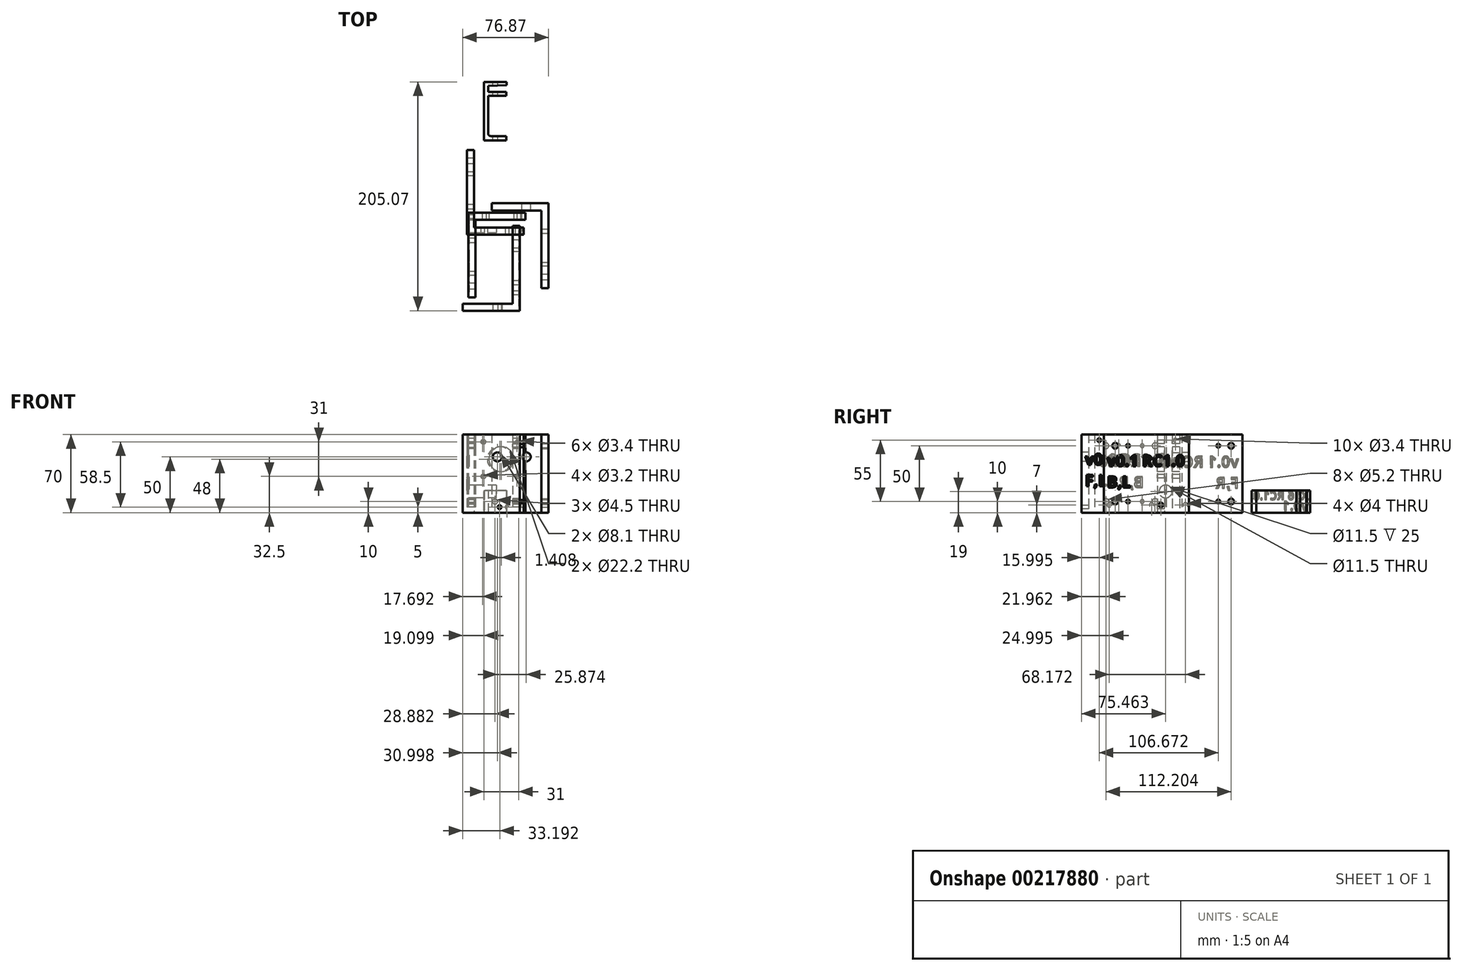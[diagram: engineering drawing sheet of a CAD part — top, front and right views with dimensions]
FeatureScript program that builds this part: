
annotation { "Feature Type Name" : "Feature", "Feature Type Description" : "" }
export const myFeature = defineFeature(function(context is Context, id is Id, definition is map)
    precondition{}
    {
        {
            var Q0;
            Q0=qCreatedBy(makeId("Top.planeOp"),FACE);
            var sketch = newSketch(context, id + "F0", { "sketchPlane" : qUnion([Q0])});
            skLineSegment(sketch, "E0.bottom", {"start": v(-23.8, 33.14) * mm, "end": v(-43.8, 33.14) * mm});
            skLineSegment(sketch, "E0.top", {"start": v(-23.8, 37.14) * mm, "end": v(-43.8, 37.14) * mm});
            skLineSegment(sketch, "E0.left", {"start": v(-23.8, 33.14) * mm, "end": v(-23.8, 37.14) * mm});
            skLineSegment(sketch, "E0.right", {"start": v(-43.8, 33.14) * mm, "end": v(-43.8, 37.14) * mm});
            skLineSegment(sketch, "E1.bottom", {"start": v(-43.8, 37.14) * mm, "end": v(-39.8, 37.14) * mm});
            skLineSegment(sketch, "E1.top", {"start": v(-43.8, 73.14) * mm, "end": v(-39.8, 73.14) * mm});
            skLineSegment(sketch, "E1.left", {"start": v(-43.8, 37.14) * mm, "end": v(-43.8, 73.14) * mm});
            skLineSegment(sketch, "E1.right", {"start": v(-39.8, 37.14) * mm, "end": v(-39.8, 73.14) * mm});
            skLineSegment(sketch, "E2.bottom", {"start": v(-43.8, 73.14) * mm, "end": v(-23.8, 73.14) * mm});
            skLineSegment(sketch, "E2.top", {"start": v(-43.8, 77.14) * mm, "end": v(-39.8, 77.14) * mm});
            skLineSegment(sketch, "E2.left", {"start": v(-43.8, 73.14) * mm, "end": v(-43.8, 77.14) * mm});
            skLineSegment(sketch, "E2.right", {"start": v(-23.8, 73.14) * mm, "end": v(-23.8, 77.14) * mm});
            skLineSegment(sketch, "E3.top", {"start": v(-43.8, 82.64) * mm, "end": v(-39.8, 82.64) * mm});
            skLineSegment(sketch, "E3.left", {"start": v(-43.8, 77.14) * mm, "end": v(-43.8, 82.64) * mm});
            skLineSegment(sketch, "E3.right", {"start": v(-39.8, 77.14) * mm, "end": v(-39.8, 82.64) * mm});
            skLineSegment(sketch, "E4.top", {"start": v(-43.8, 85.63) * mm, "end": v(-39.8, 85.63) * mm});
            skLineSegment(sketch, "E4.left", {"start": v(-43.8, 82.64) * mm, "end": v(-43.8, 85.63) * mm});
            skLineSegment(sketch, "E4.right", {"start": v(-39.8, 82.64) * mm, "end": v(-39.8, 85.63) * mm});
            skLineSegment(sketch, "E5", {"start": v(-39.8, 77.14) * mm, "end": v(-39.8, 81.94) * mm});
            skLineSegment(sketch, "E6", {"start": v(-39.8, 81.94) * mm, "end": v(-23.3, 82.64) * mm});
            skLineSegment(sketch, "E7", {"start": v(-23.3, 82.64) * mm, "end": v(-23.42, 85.63) * mm});
            skLineSegment(sketch, "E8", {"start": v(-23.42, 85.63) * mm, "end": v(-39.8, 85.63) * mm});
            skLineSegment(sketch, "E9.top", {"start": v(-23.8, 76.74) * mm, "end": v(-39.8, 76.74) * mm});
            skLineSegment(sketch, "E9.left", {"start": v(-23.8, 77.14) * mm, "end": v(-23.8, 76.74) * mm});
            skLineSegment(sketch, "E9.right", {"start": v(-39.8, 77.14) * mm, "end": v(-39.8, 76.74) * mm});
            skSolve(sketch);
        }
        {
            var Q0;
            Q0 = qSketchRegion(id + "F0", true);
            extrude(context, id + "F1", {"entities" : qUnion([Q0]), "depth" : 20 * mm});
        }
        {
            var Q0;
            Q0=makeQuery(id+"F1.opExtrude","SWEPT_FACE",FACE,{"disambiguationData":[OSD([sQuery(id+"F0.wireOp",EDGE,"E0.bottom")])]});
            var sketch = newSketch(context, id + "F2", { "sketchPlane" : qUnion([Q0])});
            skLineSegment(sketch, "E10", {"start": v(-33.8, 20) * mm, "end": v(-33.8, 10) * mm, "construction": true});
            skPoint(sketch, "E10.endSnap0", {"position": v(-23.8, 10) * mm});
            skCircle(sketch, "E11", {"center": v(-33.8, 10) * mm, "radius": 2.25 * mm});
            skSolve(sketch);
        }
        {
            var Q0;
            Q0 = qSketchRegion(id + "F2", true);
            extrude(context, id + "F3", {"entities" : qUnion([Q0]), "operationType" : NewBodyOperationType.REMOVE, "oppositeDirection" : true, "depth" : 200 * mm});
        }
        {
            var Q0;
            Q0=makeQuery(id+"F1.opExtrude","SWEPT_FACE",FACE,{"disambiguationData":[OSD([sQuery(id+"F0.wireOp",EDGE,"E0.right"),sQuery(id+"F0.wireOp",EDGE,"E1.left"),sQuery(id+"F0.wireOp",EDGE,"E2.left"),sQuery(id+"F0.wireOp",EDGE,"E3.left"),sQuery(id+"F0.wireOp",EDGE,"E4.left")])]});
            var sketch = newSketch(context, id + "F4", { "sketchPlane" : qUnion([Q0])});
            skText(sketch, "E12", { "text": "X16 RC1.0\n", "fontName": "OpenSans-Bold.ttf"});
            const initialGuessF4  = {"E12": [-0.08421, 0.01155, 1, 0, 0.00747]};
            skSetInitialGuess(sketch, initialGuessF4);
            skSolve(sketch);
        }
        {
            var Q0;
            Q0 = qSketchRegion(id + "F4", true);
            extrude(context, id + "F5", {"entities" : qUnion([Q0]), "operationType" : NewBodyOperationType.REMOVE, "oppositeDirection" : true, "depth" : .5 * mm});
        }
        {
            var Q0;
            {var subQ6=sQuery(id+"F0.wireOp",EDGE,"E4.left");var subQ8=sQuery(id+"F0.wireOp",EDGE,"E3.left");var subQ10=sQuery(id+"F0.wireOp",EDGE,"E2.left");var subQ13=sQuery(id+"F0.wireOp",EDGE,"E1.left");var subQ14=sQuery(id+"F0.wireOp",EDGE,"E0.right");var subQ17=sQuery(id+"F0.wireOp",EDGE,"E0.bottom");Q0=makeQuery(id+"F5.boolean.opBoolean","SPLIT",FACE,{"disambiguationData":[TD([makeQuery(id+"F1.opExtrude","SWEPT_FACE",FACE,{"disambiguationData":[OSD([subQ17])]})])],"derivedFrom":makeQuery(id+"F1.opExtrude","SWEPT_FACE",FACE,{"disambiguationData":[OSD([subQ14,subQ13,subQ10,subQ8,subQ6])]})});}
            var sketch = newSketch(context, id + "F6", { "sketchPlane" : qUnion([Q0])});
            skText(sketch, "E13", { "text": "v0.1", "fontName": "OpenSans-Bold.ttf"});
            const initialGuessF6  = {"E13": [-0.0841, 0.0019, 1, 0, 0.00852]};
            skSetInitialGuess(sketch, initialGuessF6);
            skSolve(sketch);
        }
        {
            var Q0;
            Q0 = qSketchRegion(id + "F6", true);
            extrude(context, id + "F7", {"entities" : qUnion([Q0]), "operationType" : NewBodyOperationType.REMOVE, "oppositeDirection" : true, "depth" : .5 * mm});
        }
        {
            var Q0;
            Q0=makeQuery(id+"F5.boolean.opBoolean","COPY",FACE,{"derivedFrom":makeQuery(id+"F5.opExtrude","CAP_FACE",FACE,{"disambiguationData":[OSD([sQuery(id+"F4.wireOp",EDGE,"E12.sketch_text.stroke-0"),sQuery(id+"F4.wireOp",EDGE,"E12.sketch_text.stroke-1"),sQuery(id+"F4.wireOp",EDGE,"E12.sketch_text.stroke-2"),sQuery(id+"F4.wireOp",EDGE,"E12.sketch_text.stroke-3"),sQuery(id+"F4.wireOp",EDGE,"E12.sketch_text.stroke-4"),sQuery(id+"F4.wireOp",EDGE,"E12.sketch_text.stroke-5"),sQuery(id+"F4.wireOp",EDGE,"E12.sketch_text.stroke-6"),sQuery(id+"F4.wireOp",EDGE,"E12.sketch_text.stroke-7"),sQuery(id+"F4.wireOp",EDGE,"E12.sketch_text.stroke-8"),sQuery(id+"F4.wireOp",EDGE,"E12.sketch_text.stroke-9"),sQuery(id+"F4.wireOp",EDGE,"E12.sketch_text.stroke-10"),sQuery(id+"F4.wireOp",EDGE,"E12.sketch_text.stroke-11")])],"isStart":false})});
            var Q1;
            Q1=makeQuery(id+"F5.boolean.opBoolean","COPY",FACE,{"derivedFrom":makeQuery(id+"F5.opExtrude","CAP_FACE",FACE,{"disambiguationData":[OSD([sQuery(id+"F4.wireOp",EDGE,"E12.sketch_text.stroke-12"),sQuery(id+"F4.wireOp",EDGE,"E12.sketch_text.stroke-13"),sQuery(id+"F4.wireOp",EDGE,"E12.sketch_text.stroke-14"),sQuery(id+"F4.wireOp",EDGE,"E12.sketch_text.stroke-15"),sQuery(id+"F4.wireOp",EDGE,"E12.sketch_text.stroke-16"),sQuery(id+"F4.wireOp",EDGE,"E12.sketch_text.stroke-17"),sQuery(id+"F4.wireOp",EDGE,"E12.sketch_text.stroke-18"),sQuery(id+"F4.wireOp",EDGE,"E12.sketch_text.stroke-19"),sQuery(id+"F4.wireOp",EDGE,"E12.sketch_text.stroke-20"),sQuery(id+"F4.wireOp",EDGE,"E12.sketch_text.stroke-21")])],"isStart":false})});
            var Q2;
            Q2=makeQuery(id+"F5.boolean.opBoolean","COPY",FACE,{"derivedFrom":makeQuery(id+"F5.opExtrude","CAP_FACE",FACE,{"disambiguationData":[OSD([sQuery(id+"F4.wireOp",EDGE,"E12.sketch_text.stroke-47"),sQuery(id+"F4.wireOp",EDGE,"E12.sketch_text.stroke-48"),sQuery(id+"F4.wireOp",EDGE,"E12.sketch_text.stroke-49"),sQuery(id+"F4.wireOp",EDGE,"E12.sketch_text.stroke-50"),sQuery(id+"F4.wireOp",EDGE,"E12.sketch_text.stroke-51"),sQuery(id+"F4.wireOp",EDGE,"E12.sketch_text.stroke-52"),sQuery(id+"F4.wireOp",EDGE,"E12.sketch_text.stroke-53"),sQuery(id+"F4.wireOp",EDGE,"E12.sketch_text.stroke-54"),sQuery(id+"F4.wireOp",EDGE,"E12.sketch_text.stroke-55"),sQuery(id+"F4.wireOp",EDGE,"E12.sketch_text.stroke-56"),sQuery(id+"F4.wireOp",EDGE,"E12.sketch_text.stroke-57"),sQuery(id+"F4.wireOp",EDGE,"E12.sketch_text.stroke-58"),sQuery(id+"F4.wireOp",EDGE,"E12.sketch_text.stroke-59"),sQuery(id+"F4.wireOp",EDGE,"E12.sketch_text.stroke-60"),sQuery(id+"F4.wireOp",EDGE,"E12.sketch_text.stroke-61"),sQuery(id+"F4.wireOp",EDGE,"E12.sketch_text.stroke-62"),sQuery(id+"F4.wireOp",EDGE,"E12.sketch_text.stroke-63"),sQuery(id+"F4.wireOp",EDGE,"E12.sketch_text.stroke-64"),sQuery(id+"F4.wireOp",EDGE,"E12.sketch_text.stroke-65")])],"isStart":false})});
            var Q3;
            Q3=makeQuery(id+"F5.boolean.opBoolean","COPY",FACE,{"derivedFrom":makeQuery(id+"F5.opExtrude","CAP_FACE",FACE,{"disambiguationData":[OSD([sQuery(id+"F4.wireOp",EDGE,"E12.sketch_text.stroke-66"),sQuery(id+"F4.wireOp",EDGE,"E12.sketch_text.stroke-67"),sQuery(id+"F4.wireOp",EDGE,"E12.sketch_text.stroke-68"),sQuery(id+"F4.wireOp",EDGE,"E12.sketch_text.stroke-69"),sQuery(id+"F4.wireOp",EDGE,"E12.sketch_text.stroke-70"),sQuery(id+"F4.wireOp",EDGE,"E12.sketch_text.stroke-71"),sQuery(id+"F4.wireOp",EDGE,"E12.sketch_text.stroke-72"),sQuery(id+"F4.wireOp",EDGE,"E12.sketch_text.stroke-73"),sQuery(id+"F4.wireOp",EDGE,"E12.sketch_text.stroke-74"),sQuery(id+"F4.wireOp",EDGE,"E12.sketch_text.stroke-75"),sQuery(id+"F4.wireOp",EDGE,"E12.sketch_text.stroke-76"),sQuery(id+"F4.wireOp",EDGE,"E12.sketch_text.stroke-77"),sQuery(id+"F4.wireOp",EDGE,"E12.sketch_text.stroke-78"),sQuery(id+"F4.wireOp",EDGE,"E12.sketch_text.stroke-79"),sQuery(id+"F4.wireOp",EDGE,"E12.sketch_text.stroke-80")])],"isStart":false})});
            var Q4;
            Q4=makeQuery(id+"F5.boolean.opBoolean","COPY",FACE,{"derivedFrom":makeQuery(id+"F5.opExtrude","CAP_FACE",FACE,{"disambiguationData":[OSD([sQuery(id+"F4.wireOp",EDGE,"E12.sketch_text.stroke-81"),sQuery(id+"F4.wireOp",EDGE,"E12.sketch_text.stroke-82"),sQuery(id+"F4.wireOp",EDGE,"E12.sketch_text.stroke-83"),sQuery(id+"F4.wireOp",EDGE,"E12.sketch_text.stroke-84"),sQuery(id+"F4.wireOp",EDGE,"E12.sketch_text.stroke-85"),sQuery(id+"F4.wireOp",EDGE,"E12.sketch_text.stroke-86"),sQuery(id+"F4.wireOp",EDGE,"E12.sketch_text.stroke-87"),sQuery(id+"F4.wireOp",EDGE,"E12.sketch_text.stroke-88"),sQuery(id+"F4.wireOp",EDGE,"E12.sketch_text.stroke-89"),sQuery(id+"F4.wireOp",EDGE,"E12.sketch_text.stroke-90")])],"isStart":false})});
            var Q5;
            Q5=makeQuery(id+"F5.boolean.opBoolean","COPY",FACE,{"derivedFrom":makeQuery(id+"F5.opExtrude","CAP_FACE",FACE,{"disambiguationData":[OSD([sQuery(id+"F4.wireOp",EDGE,"E12.sketch_text.stroke-99"),sQuery(id+"F4.wireOp",EDGE,"E12.sketch_text.stroke-100"),sQuery(id+"F4.wireOp",EDGE,"E12.sketch_text.stroke-101"),sQuery(id+"F4.wireOp",EDGE,"E12.sketch_text.stroke-102"),sQuery(id+"F4.wireOp",EDGE,"E12.sketch_text.stroke-103"),sQuery(id+"F4.wireOp",EDGE,"E12.sketch_text.stroke-104"),sQuery(id+"F4.wireOp",EDGE,"E12.sketch_text.stroke-105"),sQuery(id+"F4.wireOp",EDGE,"E12.sketch_text.stroke-106"),sQuery(id+"F4.wireOp",EDGE,"E12.sketch_text.stroke-107"),sQuery(id+"F4.wireOp",EDGE,"E12.sketch_text.stroke-108"),sQuery(id+"F4.wireOp",EDGE,"E12.sketch_text.stroke-109"),sQuery(id+"F4.wireOp",EDGE,"E12.sketch_text.stroke-110"),sQuery(id+"F4.wireOp",EDGE,"E12.sketch_text.stroke-111"),sQuery(id+"F4.wireOp",EDGE,"E12.sketch_text.stroke-112"),sQuery(id+"F4.wireOp",EDGE,"E12.sketch_text.stroke-113"),sQuery(id+"F4.wireOp",EDGE,"E12.sketch_text.stroke-114")])],"isStart":false})});
            var Q6;
            Q6=makeQuery(id+"F5.boolean.opBoolean","COPY",FACE,{"derivedFrom":makeQuery(id+"F5.opExtrude","CAP_FACE",FACE,{"disambiguationData":[OSD([sQuery(id+"F4.wireOp",EDGE,"E12.sketch_text.stroke-91"),sQuery(id+"F4.wireOp",EDGE,"E12.sketch_text.stroke-92"),sQuery(id+"F4.wireOp",EDGE,"E12.sketch_text.stroke-93"),sQuery(id+"F4.wireOp",EDGE,"E12.sketch_text.stroke-94"),sQuery(id+"F4.wireOp",EDGE,"E12.sketch_text.stroke-95"),sQuery(id+"F4.wireOp",EDGE,"E12.sketch_text.stroke-96"),sQuery(id+"F4.wireOp",EDGE,"E12.sketch_text.stroke-97"),sQuery(id+"F4.wireOp",EDGE,"E12.sketch_text.stroke-98")])],"isStart":false})});
            var Q7;
            Q7=makeQuery(id+"F7.boolean.opBoolean","COPY",FACE,{"derivedFrom":makeQuery(id+"F7.opExtrude","CAP_FACE",FACE,{"disambiguationData":[OSD([sQuery(id+"F6.wireOp",EDGE,"E13.sketch_text.stroke-34"),sQuery(id+"F6.wireOp",EDGE,"E13.sketch_text.stroke-35"),sQuery(id+"F6.wireOp",EDGE,"E13.sketch_text.stroke-36"),sQuery(id+"F6.wireOp",EDGE,"E13.sketch_text.stroke-37"),sQuery(id+"F6.wireOp",EDGE,"E13.sketch_text.stroke-38"),sQuery(id+"F6.wireOp",EDGE,"E13.sketch_text.stroke-39"),sQuery(id+"F6.wireOp",EDGE,"E13.sketch_text.stroke-40"),sQuery(id+"F6.wireOp",EDGE,"E13.sketch_text.stroke-41"),sQuery(id+"F6.wireOp",EDGE,"E13.sketch_text.stroke-42"),sQuery(id+"F6.wireOp",EDGE,"E13.sketch_text.stroke-43")])],"isStart":false})});
            var Q8;
            Q8=makeQuery(id+"F7.boolean.opBoolean","COPY",FACE,{"derivedFrom":makeQuery(id+"F7.opExtrude","CAP_FACE",FACE,{"disambiguationData":[OSD([sQuery(id+"F6.wireOp",EDGE,"E13.sketch_text.stroke-10"),sQuery(id+"F6.wireOp",EDGE,"E13.sketch_text.stroke-11"),sQuery(id+"F6.wireOp",EDGE,"E13.sketch_text.stroke-12"),sQuery(id+"F6.wireOp",EDGE,"E13.sketch_text.stroke-13"),sQuery(id+"F6.wireOp",EDGE,"E13.sketch_text.stroke-14"),sQuery(id+"F6.wireOp",EDGE,"E13.sketch_text.stroke-15"),sQuery(id+"F6.wireOp",EDGE,"E13.sketch_text.stroke-16"),sQuery(id+"F6.wireOp",EDGE,"E13.sketch_text.stroke-17"),sQuery(id+"F6.wireOp",EDGE,"E13.sketch_text.stroke-18"),sQuery(id+"F6.wireOp",EDGE,"E13.sketch_text.stroke-19"),sQuery(id+"F6.wireOp",EDGE,"E13.sketch_text.stroke-20"),sQuery(id+"F6.wireOp",EDGE,"E13.sketch_text.stroke-21"),sQuery(id+"F6.wireOp",EDGE,"E13.sketch_text.stroke-22"),sQuery(id+"F6.wireOp",EDGE,"E13.sketch_text.stroke-23"),sQuery(id+"F6.wireOp",EDGE,"E13.sketch_text.stroke-24"),sQuery(id+"F6.wireOp",EDGE,"E13.sketch_text.stroke-25")])],"isStart":false})});
            var Q9;
            Q9=makeQuery(id+"F7.boolean.opBoolean","COPY",FACE,{"derivedFrom":makeQuery(id+"F7.opExtrude","CAP_FACE",FACE,{"disambiguationData":[OSD([sQuery(id+"F6.wireOp",EDGE,"E13.sketch_text.stroke-26"),sQuery(id+"F6.wireOp",EDGE,"E13.sketch_text.stroke-27"),sQuery(id+"F6.wireOp",EDGE,"E13.sketch_text.stroke-28"),sQuery(id+"F6.wireOp",EDGE,"E13.sketch_text.stroke-29"),sQuery(id+"F6.wireOp",EDGE,"E13.sketch_text.stroke-30"),sQuery(id+"F6.wireOp",EDGE,"E13.sketch_text.stroke-31"),sQuery(id+"F6.wireOp",EDGE,"E13.sketch_text.stroke-32"),sQuery(id+"F6.wireOp",EDGE,"E13.sketch_text.stroke-33")])],"isStart":false})});
            var Q10;
            Q10=makeQuery(id+"F7.boolean.opBoolean","COPY",FACE,{"derivedFrom":makeQuery(id+"F7.opExtrude","CAP_FACE",FACE,{"disambiguationData":[OSD([sQuery(id+"F6.wireOp",EDGE,"E13.sketch_text.stroke-0"),sQuery(id+"F6.wireOp",EDGE,"E13.sketch_text.stroke-1"),sQuery(id+"F6.wireOp",EDGE,"E13.sketch_text.stroke-2"),sQuery(id+"F6.wireOp",EDGE,"E13.sketch_text.stroke-3"),sQuery(id+"F6.wireOp",EDGE,"E13.sketch_text.stroke-4"),sQuery(id+"F6.wireOp",EDGE,"E13.sketch_text.stroke-5"),sQuery(id+"F6.wireOp",EDGE,"E13.sketch_text.stroke-6"),sQuery(id+"F6.wireOp",EDGE,"E13.sketch_text.stroke-7"),sQuery(id+"F6.wireOp",EDGE,"E13.sketch_text.stroke-8"),sQuery(id+"F6.wireOp",EDGE,"E13.sketch_text.stroke-9")])],"isStart":false})});
            chamfer(context, id + "F8", {"entities" : qUnion([Q0, Q1, Q2, Q3, Q4, Q5, Q6, Q7, Q8, Q9, Q10]), "width" : .5 * mm, "tangentPropagation" : true});
        }
        {
            var Q0;
            Q0=makeQuery(id+"F5.boolean.opBoolean","COPY",FACE,{"derivedFrom":makeQuery(id+"F5.opExtrude","CAP_FACE",FACE,{"disambiguationData":[OSD([sQuery(id+"F4.wireOp",EDGE,"E12.sketch_text.stroke-22"),sQuery(id+"F4.wireOp",EDGE,"E12.sketch_text.stroke-23"),sQuery(id+"F4.wireOp",EDGE,"E12.sketch_text.stroke-24"),sQuery(id+"F4.wireOp",EDGE,"E12.sketch_text.stroke-25"),sQuery(id+"F4.wireOp",EDGE,"E12.sketch_text.stroke-26"),sQuery(id+"F4.wireOp",EDGE,"E12.sketch_text.stroke-27"),sQuery(id+"F4.wireOp",EDGE,"E12.sketch_text.stroke-28"),sQuery(id+"F4.wireOp",EDGE,"E12.sketch_text.stroke-29"),sQuery(id+"F4.wireOp",EDGE,"E12.sketch_text.stroke-30"),sQuery(id+"F4.wireOp",EDGE,"E12.sketch_text.stroke-31"),sQuery(id+"F4.wireOp",EDGE,"E12.sketch_text.stroke-32"),sQuery(id+"F4.wireOp",EDGE,"E12.sketch_text.stroke-33"),sQuery(id+"F4.wireOp",EDGE,"E12.sketch_text.stroke-34"),sQuery(id+"F4.wireOp",EDGE,"E12.sketch_text.stroke-35"),sQuery(id+"F4.wireOp",EDGE,"E12.sketch_text.stroke-36"),sQuery(id+"F4.wireOp",EDGE,"E12.sketch_text.stroke-37"),sQuery(id+"F4.wireOp",EDGE,"E12.sketch_text.stroke-38"),sQuery(id+"F4.wireOp",EDGE,"E12.sketch_text.stroke-39"),sQuery(id+"F4.wireOp",EDGE,"E12.sketch_text.stroke-40"),sQuery(id+"F4.wireOp",EDGE,"E12.sketch_text.stroke-41"),sQuery(id+"F4.wireOp",EDGE,"E12.sketch_text.stroke-42"),sQuery(id+"F4.wireOp",EDGE,"E12.sketch_text.stroke-43"),sQuery(id+"F4.wireOp",EDGE,"E12.sketch_text.stroke-44"),sQuery(id+"F4.wireOp",EDGE,"E12.sketch_text.stroke-45"),sQuery(id+"F4.wireOp",EDGE,"E12.sketch_text.stroke-46")])],"isStart":false})});
            chamfer(context, id + "F9", {"entities" : qUnion([Q0]), "chamferType" : ChamferType.TWO_OFFSETS, "width1" : .5 * mm, "oppositeDirection" : false, "width2" : .3 * mm, "tangentPropagation" : true});
        }
        {
            var Q0;
            Q0=makeQuery(id+"F1.opExtrude","SWEPT_EDGE",EDGE,{"disambiguationData":[OSD([sQuery(id+"F0.wireOp",EDGE,"E0.top"),sQuery(id+"F0.wireOp",EDGE,"E1.bottom"),sQuery(id+"F0.wireOp",EDGE,"E1.right")])]});
            fillet(context, id + "F10", {"entities" : qUnion([Q0]), "radius" : 2 * mm, "tangentPropagation" : true, "allowEdgeOverflow" : false});
        }
        {
            var Q0;
            Q0=qCreatedBy(makeId("Top.planeOp"),FACE);
            var sketch = newSketch(context, id + "F11", { "sketchPlane" : qUnion([Q0])});
            skLineSegment(sketch, "E14", {"start": v(-59, 24.73) * mm, "end": v(-52.6, 24.73) * mm});
            skLineSegment(sketch, "E15", {"start": v(-59, 24.73) * mm, "end": v(-59, -51.27) * mm});
            skLineSegment(sketch, "E16", {"start": v(-59, -51.27) * mm, "end": v(-8, -51.27) * mm});
            skLineSegment(sketch, "E17", {"start": v(-8, -51.27) * mm, "end": v(-8, -44.87) * mm});
            skLineSegment(sketch, "E18", {"start": v(-8, -44.87) * mm, "end": v(-52.6, -44.87) * mm});
            skLineSegment(sketch, "E19", {"start": v(-52.6, -44.87) * mm, "end": v(-52.6, 24.73) * mm});
            skSolve(sketch);
        }
        {
            var Q0;
            Q0 = qSketchRegion(id + "F11", true);
            extrude(context, id + "F12", {"entities" : qUnion([Q0]), "depth" : 70 * mm});
        }
        {
            var Q0;
            Q0=makeQuery(id+"F12.opExtrude","SWEPT_FACE",FACE,{"disambiguationData":[OSD([sQuery(id+"F11.wireOp",EDGE,"E16")])]});
            var sketch = newSketch(context, id + "F13", { "sketchPlane" : qUnion([Q0])});
            skLineSegment(sketch, "E20", {"start": v(-59, 70) * mm, "end": v(-29.5, 70) * mm, "construction": true});
            skLineSegment(sketch, "E21", {"start": v(-29.5, 70) * mm, "end": v(-29.5, 48) * mm, "construction": true});
            skCircle(sketch, "E22", {"center": v(-29.5, 48) * mm, "radius": 11.1 * mm});
            skLineSegment(sketch, "E23", {"start": v(-29.5, 48) * mm, "end": v(-29.5, 63.5) * mm, "construction": true});
            skLineSegment(sketch, "E24", {"start": v(-29.5, 63.5) * mm, "end": v(-14, 63.5) * mm, "construction": true});
            skLineSegment(sketch, "E25", {"start": v(-14, 63.5) * mm, "end": v(-14, 32.5) * mm, "construction": true});
            skLineSegment(sketch, "E26", {"start": v(-14, 32.5) * mm, "end": v(-45, 32.5) * mm, "construction": true});
            skLineSegment(sketch, "E27", {"start": v(-45, 32.5) * mm, "end": v(-45, 63.5) * mm, "construction": true});
            skCircle(sketch, "E28", {"center": v(-14, 63.5) * mm, "radius": 1.6 * mm});
            skCircle(sketch, "E29", {"center": v(-45, 63.5) * mm, "radius": 1.6 * mm});
            skCircle(sketch, "E30", {"center": v(-45, 32.5) * mm, "radius": 1.6 * mm});
            skCircle(sketch, "E31", {"center": v(-14, 32.5) * mm, "radius": 1.6 * mm});
            skLineSegment(sketch, "E32", {"start": v(-59, 0) * mm, "end": v(-23, 0) * mm, "construction": true});
            skLineSegment(sketch, "E33", {"start": v(-23, 0) * mm, "end": v(-23, 5) * mm, "construction": true});
            skCircle(sketch, "E34", {"center": v(-23, 5) * mm, "radius": 1.7 * mm});
            skSolve(sketch);
        }
        {
            var Q0;
            Q0 = qSketchRegion(id + "F13", true);
            extrude(context, id + "F14", {"entities" : qUnion([Q0]), "operationType" : NewBodyOperationType.REMOVE, "oppositeDirection" : true, "depth" : 25 * mm});
        }
        {
            var Q0;
            Q0=makeQuery(id+"F12.opExtrude","SWEPT_FACE",FACE,{"disambiguationData":[OSD([sQuery(id+"F11.wireOp",EDGE,"E15")])]});
            var sketch = newSketch(context, id + "F15", { "sketchPlane" : qUnion([Q0])});
            skLineSegment(sketch, "E35", {"start": v(-24.73, 0) * mm, "end": v(-14.73, 0) * mm, "construction": true});
            skLineSegment(sketch, "E36", {"start": v(-14.73, 0) * mm, "end": v(-3.23, 0) * mm, "construction": true});
            skLineSegment(sketch, "E37", {"start": v(-14.73, 0) * mm, "end": v(-14.73, 10) * mm, "construction": true});
            skLineSegment(sketch, "E38", {"start": v(-24.73, 70) * mm, "end": v(-14.73, 70) * mm, "construction": true});
            skLineSegment(sketch, "E39", {"start": v(-14.73, 70) * mm, "end": v(-14.73, 60) * mm, "construction": true});
            skCircle(sketch, "E40", {"center": v(-14.73, 60) * mm, "radius": 2.6 * mm});
            skCircle(sketch, "E41", {"center": v(-14.73, 10) * mm, "radius": 2.6 * mm});
            skLineSegment(sketch, "E42", {"start": v(-3.23, 0) * mm, "end": v(-3.23, 10) * mm, "construction": true});
            skLineSegment(sketch, "E43", {"start": v(-3.23, 0) * mm, "end": v(26.27, 0) * mm, "construction": true});
            skLineSegment(sketch, "E44", {"start": v(26.27, 0) * mm, "end": v(26.27, 7) * mm, "construction": true});
            skCircle(sketch, "E45", {"center": v(26.27, 7) * mm, "radius": 2 * mm});
            skCircle(sketch, "E46", {"center": v(-3.23, 10) * mm, "radius": 1.7 * mm});
            skLineSegment(sketch, "E47", {"start": v(-14.73, 70) * mm, "end": v(-3.23, 70) * mm, "construction": true});
            skLineSegment(sketch, "E48", {"start": v(-3.23, 70) * mm, "end": v(-3.23, 60) * mm, "construction": true});
            skCircle(sketch, "E49", {"center": v(-3.23, 60) * mm, "radius": 1.7 * mm});
            skLineSegment(sketch, "E50", {"start": v(-3.23, 70) * mm, "end": v(35.27, 70) * mm, "construction": true});
            skLineSegment(sketch, "E51", {"start": v(35.27, 70) * mm, "end": v(35.27, 65) * mm, "construction": true});
            skCircle(sketch, "E52", {"center": v(35.27, 65) * mm, "radius": 1.7 * mm});
            skSolve(sketch);
        }
        {
            var Q0;
            Q0 = qSketchRegion(id + "F15", true);
            extrude(context, id + "F16", {"entities" : qUnion([Q0]), "operationType" : NewBodyOperationType.REMOVE, "oppositeDirection" : true, "depth" : 25 * mm});
        }
        {
            var Q0;
            Q0=makeQuery(id+"F12.opExtrude","SWEPT_FACE",FACE,{"disambiguationData":[OSD([sQuery(id+"F11.wireOp",EDGE,"E15")])]});
            var sketch = newSketch(context, id + "F17", { "sketchPlane" : qUnion([Q0])});
            skText(sketch, "E53", { "text": "v0.1 RC1.0\nF,R", "fontName": "OpenSans-Bold.ttf"});
            const initialGuessF17  = {"E53": [-0.02176, 0.04067, 1, 0, 0.01006]};
            skSetInitialGuess(sketch, initialGuessF17);
            skSolve(sketch);
        }
        {
            var Q0;
            Q0 = qSketchRegion(id + "F17", true);
            extrude(context, id + "F18", {"entities" : qUnion([Q0]), "operationType" : NewBodyOperationType.REMOVE, "oppositeDirection" : true, "depth" : .5 * mm});
        }
        {
            var Q0;
            Q0=makeQuery(id+"F18.boolean.opBoolean","COPY",FACE,{"derivedFrom":makeQuery(id+"F18.opExtrude","CAP_FACE",FACE,{"disambiguationData":[OSD([sQuery(id+"F17.wireOp",EDGE,"E53.sketch_text.stroke-0"),sQuery(id+"F17.wireOp",EDGE,"E53.sketch_text.stroke-1"),sQuery(id+"F17.wireOp",EDGE,"E53.sketch_text.stroke-2"),sQuery(id+"F17.wireOp",EDGE,"E53.sketch_text.stroke-3"),sQuery(id+"F17.wireOp",EDGE,"E53.sketch_text.stroke-4"),sQuery(id+"F17.wireOp",EDGE,"E53.sketch_text.stroke-5"),sQuery(id+"F17.wireOp",EDGE,"E53.sketch_text.stroke-6"),sQuery(id+"F17.wireOp",EDGE,"E53.sketch_text.stroke-7"),sQuery(id+"F17.wireOp",EDGE,"E53.sketch_text.stroke-8"),sQuery(id+"F17.wireOp",EDGE,"E53.sketch_text.stroke-9")])],"isStart":false})});
            var Q1;
            Q1=makeQuery(id+"F18.boolean.opBoolean","COPY",FACE,{"derivedFrom":makeQuery(id+"F18.opExtrude","CAP_FACE",FACE,{"disambiguationData":[OSD([sQuery(id+"F17.wireOp",EDGE,"E53.sketch_text.stroke-10"),sQuery(id+"F17.wireOp",EDGE,"E53.sketch_text.stroke-11"),sQuery(id+"F17.wireOp",EDGE,"E53.sketch_text.stroke-12"),sQuery(id+"F17.wireOp",EDGE,"E53.sketch_text.stroke-13"),sQuery(id+"F17.wireOp",EDGE,"E53.sketch_text.stroke-14"),sQuery(id+"F17.wireOp",EDGE,"E53.sketch_text.stroke-15"),sQuery(id+"F17.wireOp",EDGE,"E53.sketch_text.stroke-16"),sQuery(id+"F17.wireOp",EDGE,"E53.sketch_text.stroke-17"),sQuery(id+"F17.wireOp",EDGE,"E53.sketch_text.stroke-18"),sQuery(id+"F17.wireOp",EDGE,"E53.sketch_text.stroke-19"),sQuery(id+"F17.wireOp",EDGE,"E53.sketch_text.stroke-20"),sQuery(id+"F17.wireOp",EDGE,"E53.sketch_text.stroke-21"),sQuery(id+"F17.wireOp",EDGE,"E53.sketch_text.stroke-22"),sQuery(id+"F17.wireOp",EDGE,"E53.sketch_text.stroke-23"),sQuery(id+"F17.wireOp",EDGE,"E53.sketch_text.stroke-24"),sQuery(id+"F17.wireOp",EDGE,"E53.sketch_text.stroke-25")])],"isStart":false})});
            var Q2;
            Q2=makeQuery(id+"F18.boolean.opBoolean","COPY",FACE,{"derivedFrom":makeQuery(id+"F18.opExtrude","CAP_FACE",FACE,{"disambiguationData":[OSD([sQuery(id+"F17.wireOp",EDGE,"E53.sketch_text.stroke-34"),sQuery(id+"F17.wireOp",EDGE,"E53.sketch_text.stroke-35"),sQuery(id+"F17.wireOp",EDGE,"E53.sketch_text.stroke-36"),sQuery(id+"F17.wireOp",EDGE,"E53.sketch_text.stroke-37"),sQuery(id+"F17.wireOp",EDGE,"E53.sketch_text.stroke-38"),sQuery(id+"F17.wireOp",EDGE,"E53.sketch_text.stroke-39"),sQuery(id+"F17.wireOp",EDGE,"E53.sketch_text.stroke-40"),sQuery(id+"F17.wireOp",EDGE,"E53.sketch_text.stroke-41"),sQuery(id+"F17.wireOp",EDGE,"E53.sketch_text.stroke-42"),sQuery(id+"F17.wireOp",EDGE,"E53.sketch_text.stroke-43")])],"isStart":false})});
            var Q3;
            Q3=makeQuery(id+"F18.boolean.opBoolean","COPY",FACE,{"derivedFrom":makeQuery(id+"F18.opExtrude","CAP_FACE",FACE,{"disambiguationData":[OSD([sQuery(id+"F17.wireOp",EDGE,"E53.sketch_text.stroke-44"),sQuery(id+"F17.wireOp",EDGE,"E53.sketch_text.stroke-45"),sQuery(id+"F17.wireOp",EDGE,"E53.sketch_text.stroke-46"),sQuery(id+"F17.wireOp",EDGE,"E53.sketch_text.stroke-47"),sQuery(id+"F17.wireOp",EDGE,"E53.sketch_text.stroke-48"),sQuery(id+"F17.wireOp",EDGE,"E53.sketch_text.stroke-49"),sQuery(id+"F17.wireOp",EDGE,"E53.sketch_text.stroke-50"),sQuery(id+"F17.wireOp",EDGE,"E53.sketch_text.stroke-51"),sQuery(id+"F17.wireOp",EDGE,"E53.sketch_text.stroke-52"),sQuery(id+"F17.wireOp",EDGE,"E53.sketch_text.stroke-53"),sQuery(id+"F17.wireOp",EDGE,"E53.sketch_text.stroke-54"),sQuery(id+"F17.wireOp",EDGE,"E53.sketch_text.stroke-55"),sQuery(id+"F17.wireOp",EDGE,"E53.sketch_text.stroke-56"),sQuery(id+"F17.wireOp",EDGE,"E53.sketch_text.stroke-57"),sQuery(id+"F17.wireOp",EDGE,"E53.sketch_text.stroke-58"),sQuery(id+"F17.wireOp",EDGE,"E53.sketch_text.stroke-59"),sQuery(id+"F17.wireOp",EDGE,"E53.sketch_text.stroke-60"),sQuery(id+"F17.wireOp",EDGE,"E53.sketch_text.stroke-61"),sQuery(id+"F17.wireOp",EDGE,"E53.sketch_text.stroke-62")])],"isStart":false})});
            var Q4;
            Q4=makeQuery(id+"F18.boolean.opBoolean","COPY",FACE,{"derivedFrom":makeQuery(id+"F18.opExtrude","CAP_FACE",FACE,{"disambiguationData":[OSD([sQuery(id+"F17.wireOp",EDGE,"E53.sketch_text.stroke-63"),sQuery(id+"F17.wireOp",EDGE,"E53.sketch_text.stroke-64"),sQuery(id+"F17.wireOp",EDGE,"E53.sketch_text.stroke-65"),sQuery(id+"F17.wireOp",EDGE,"E53.sketch_text.stroke-66"),sQuery(id+"F17.wireOp",EDGE,"E53.sketch_text.stroke-67"),sQuery(id+"F17.wireOp",EDGE,"E53.sketch_text.stroke-68"),sQuery(id+"F17.wireOp",EDGE,"E53.sketch_text.stroke-69"),sQuery(id+"F17.wireOp",EDGE,"E53.sketch_text.stroke-70"),sQuery(id+"F17.wireOp",EDGE,"E53.sketch_text.stroke-71"),sQuery(id+"F17.wireOp",EDGE,"E53.sketch_text.stroke-72"),sQuery(id+"F17.wireOp",EDGE,"E53.sketch_text.stroke-73"),sQuery(id+"F17.wireOp",EDGE,"E53.sketch_text.stroke-74"),sQuery(id+"F17.wireOp",EDGE,"E53.sketch_text.stroke-75"),sQuery(id+"F17.wireOp",EDGE,"E53.sketch_text.stroke-76"),sQuery(id+"F17.wireOp",EDGE,"E53.sketch_text.stroke-77")])],"isStart":false})});
            var Q5;
            Q5=makeQuery(id+"F18.boolean.opBoolean","COPY",FACE,{"derivedFrom":makeQuery(id+"F18.opExtrude","CAP_FACE",FACE,{"disambiguationData":[OSD([sQuery(id+"F17.wireOp",EDGE,"E53.sketch_text.stroke-78"),sQuery(id+"F17.wireOp",EDGE,"E53.sketch_text.stroke-79"),sQuery(id+"F17.wireOp",EDGE,"E53.sketch_text.stroke-80"),sQuery(id+"F17.wireOp",EDGE,"E53.sketch_text.stroke-81"),sQuery(id+"F17.wireOp",EDGE,"E53.sketch_text.stroke-82"),sQuery(id+"F17.wireOp",EDGE,"E53.sketch_text.stroke-83"),sQuery(id+"F17.wireOp",EDGE,"E53.sketch_text.stroke-84"),sQuery(id+"F17.wireOp",EDGE,"E53.sketch_text.stroke-85"),sQuery(id+"F17.wireOp",EDGE,"E53.sketch_text.stroke-86"),sQuery(id+"F17.wireOp",EDGE,"E53.sketch_text.stroke-87")])],"isStart":false})});
            var Q6;
            Q6=makeQuery(id+"F18.boolean.opBoolean","COPY",FACE,{"derivedFrom":makeQuery(id+"F18.opExtrude","CAP_FACE",FACE,{"disambiguationData":[OSD([sQuery(id+"F17.wireOp",EDGE,"E53.sketch_text.stroke-96"),sQuery(id+"F17.wireOp",EDGE,"E53.sketch_text.stroke-97"),sQuery(id+"F17.wireOp",EDGE,"E53.sketch_text.stroke-98"),sQuery(id+"F17.wireOp",EDGE,"E53.sketch_text.stroke-99"),sQuery(id+"F17.wireOp",EDGE,"E53.sketch_text.stroke-100"),sQuery(id+"F17.wireOp",EDGE,"E53.sketch_text.stroke-101"),sQuery(id+"F17.wireOp",EDGE,"E53.sketch_text.stroke-102"),sQuery(id+"F17.wireOp",EDGE,"E53.sketch_text.stroke-103"),sQuery(id+"F17.wireOp",EDGE,"E53.sketch_text.stroke-104"),sQuery(id+"F17.wireOp",EDGE,"E53.sketch_text.stroke-105"),sQuery(id+"F17.wireOp",EDGE,"E53.sketch_text.stroke-106"),sQuery(id+"F17.wireOp",EDGE,"E53.sketch_text.stroke-107"),sQuery(id+"F17.wireOp",EDGE,"E53.sketch_text.stroke-108"),sQuery(id+"F17.wireOp",EDGE,"E53.sketch_text.stroke-109"),sQuery(id+"F17.wireOp",EDGE,"E53.sketch_text.stroke-110"),sQuery(id+"F17.wireOp",EDGE,"E53.sketch_text.stroke-111")])],"isStart":false})});
            var Q7;
            Q7=makeQuery(id+"F18.boolean.opBoolean","COPY",FACE,{"derivedFrom":makeQuery(id+"F18.opExtrude","CAP_FACE",FACE,{"disambiguationData":[OSD([sQuery(id+"F17.wireOp",EDGE,"E53.sketch_text.stroke-88"),sQuery(id+"F17.wireOp",EDGE,"E53.sketch_text.stroke-89"),sQuery(id+"F17.wireOp",EDGE,"E53.sketch_text.stroke-90"),sQuery(id+"F17.wireOp",EDGE,"E53.sketch_text.stroke-91"),sQuery(id+"F17.wireOp",EDGE,"E53.sketch_text.stroke-92"),sQuery(id+"F17.wireOp",EDGE,"E53.sketch_text.stroke-93"),sQuery(id+"F17.wireOp",EDGE,"E53.sketch_text.stroke-94"),sQuery(id+"F17.wireOp",EDGE,"E53.sketch_text.stroke-95")])],"isStart":false})});
            var Q8;
            Q8=makeQuery(id+"F18.boolean.opBoolean","COPY",FACE,{"derivedFrom":makeQuery(id+"F18.opExtrude","CAP_FACE",FACE,{"disambiguationData":[OSD([sQuery(id+"F17.wireOp",EDGE,"E53.sketch_text.stroke-26"),sQuery(id+"F17.wireOp",EDGE,"E53.sketch_text.stroke-27"),sQuery(id+"F17.wireOp",EDGE,"E53.sketch_text.stroke-28"),sQuery(id+"F17.wireOp",EDGE,"E53.sketch_text.stroke-29"),sQuery(id+"F17.wireOp",EDGE,"E53.sketch_text.stroke-30"),sQuery(id+"F17.wireOp",EDGE,"E53.sketch_text.stroke-31"),sQuery(id+"F17.wireOp",EDGE,"E53.sketch_text.stroke-32"),sQuery(id+"F17.wireOp",EDGE,"E53.sketch_text.stroke-33")])],"isStart":false})});
            var Q9;
            Q9=makeQuery(id+"F18.boolean.opBoolean","COPY",FACE,{"derivedFrom":makeQuery(id+"F18.opExtrude","CAP_FACE",FACE,{"disambiguationData":[OSD([sQuery(id+"F17.wireOp",EDGE,"E53.sketch_text.stroke-127"),sQuery(id+"F17.wireOp",EDGE,"E53.sketch_text.stroke-128"),sQuery(id+"F17.wireOp",EDGE,"E53.sketch_text.stroke-129"),sQuery(id+"F17.wireOp",EDGE,"E53.sketch_text.stroke-130"),sQuery(id+"F17.wireOp",EDGE,"E53.sketch_text.stroke-131"),sQuery(id+"F17.wireOp",EDGE,"E53.sketch_text.stroke-132"),sQuery(id+"F17.wireOp",EDGE,"E53.sketch_text.stroke-133"),sQuery(id+"F17.wireOp",EDGE,"E53.sketch_text.stroke-134"),sQuery(id+"F17.wireOp",EDGE,"E53.sketch_text.stroke-135"),sQuery(id+"F17.wireOp",EDGE,"E53.sketch_text.stroke-136"),sQuery(id+"F17.wireOp",EDGE,"E53.sketch_text.stroke-137"),sQuery(id+"F17.wireOp",EDGE,"E53.sketch_text.stroke-138"),sQuery(id+"F17.wireOp",EDGE,"E53.sketch_text.stroke-139"),sQuery(id+"F17.wireOp",EDGE,"E53.sketch_text.stroke-140"),sQuery(id+"F17.wireOp",EDGE,"E53.sketch_text.stroke-141"),sQuery(id+"F17.wireOp",EDGE,"E53.sketch_text.stroke-142"),sQuery(id+"F17.wireOp",EDGE,"E53.sketch_text.stroke-143"),sQuery(id+"F17.wireOp",EDGE,"E53.sketch_text.stroke-144"),sQuery(id+"F17.wireOp",EDGE,"E53.sketch_text.stroke-145")])],"isStart":false})});
            var Q10;
            Q10=makeQuery(id+"F18.boolean.opBoolean","COPY",FACE,{"derivedFrom":makeQuery(id+"F18.opExtrude","CAP_FACE",FACE,{"disambiguationData":[OSD([sQuery(id+"F17.wireOp",EDGE,"E53.sketch_text.stroke-122"),sQuery(id+"F17.wireOp",EDGE,"E53.sketch_text.stroke-123"),sQuery(id+"F17.wireOp",EDGE,"E53.sketch_text.stroke-124"),sQuery(id+"F17.wireOp",EDGE,"E53.sketch_text.stroke-125"),sQuery(id+"F17.wireOp",EDGE,"E53.sketch_text.stroke-126")])],"isStart":false})});
            var Q11;
            Q11=makeQuery(id+"F18.boolean.opBoolean","COPY",FACE,{"derivedFrom":makeQuery(id+"F18.opExtrude","CAP_FACE",FACE,{"disambiguationData":[OSD([sQuery(id+"F17.wireOp",EDGE,"E53.sketch_text.stroke-112"),sQuery(id+"F17.wireOp",EDGE,"E53.sketch_text.stroke-113"),sQuery(id+"F17.wireOp",EDGE,"E53.sketch_text.stroke-114"),sQuery(id+"F17.wireOp",EDGE,"E53.sketch_text.stroke-115"),sQuery(id+"F17.wireOp",EDGE,"E53.sketch_text.stroke-116"),sQuery(id+"F17.wireOp",EDGE,"E53.sketch_text.stroke-117"),sQuery(id+"F17.wireOp",EDGE,"E53.sketch_text.stroke-118"),sQuery(id+"F17.wireOp",EDGE,"E53.sketch_text.stroke-119"),sQuery(id+"F17.wireOp",EDGE,"E53.sketch_text.stroke-120"),sQuery(id+"F17.wireOp",EDGE,"E53.sketch_text.stroke-121")])],"isStart":false})});
            chamfer(context, id + "F19", {"entities" : qUnion([Q0, Q1, Q2, Q3, Q4, Q5, Q6, Q7, Q8, Q9, Q10, Q11]), "width" : .5 * mm, "tangentPropagation" : true});
        }
        {
            var Q0;
            Q0=qCreatedBy(makeId("Top.planeOp"),FACE);
            var sketch = newSketch(context, id + "F20", { "sketchPlane" : qUnion([Q0])});
            skLineSegment(sketch, "E54", {"start": v(-57.6, -31.48) * mm, "end": v(-6.6, -31.48) * mm});
            skLineSegment(sketch, "E55", {"start": v(-6.6, -31.48) * mm, "end": v(-6.6, -37.88) * mm});
            skLineSegment(sketch, "E56", {"start": v(-57.6, -31.48) * mm, "end": v(-57.6, -107.48) * mm});
            skLineSegment(sketch, "E57", {"start": v(-57.6, -107.48) * mm, "end": v(-51.2, -107.48) * mm});
            skLineSegment(sketch, "E58", {"start": v(-51.2, -107.48) * mm, "end": v(-51.2, -37.88) * mm});
            skLineSegment(sketch, "E59", {"start": v(-51.2, -37.88) * mm, "end": v(-6.6, -37.88) * mm});
            skSolve(sketch);
        }
        {
            var Q0;
            Q0 = qSketchRegion(id + "F20", true);
            extrude(context, id + "F21", {"entities" : qUnion([Q0]), "depth" : 70 * mm});
        }
        {
            var Q0;
            Q0=makeQuery(id+"F21.opExtrude","SWEPT_FACE",FACE,{"disambiguationData":[OSD([sQuery(id+"F20.wireOp",EDGE,"E59")])]});
            var sketch = newSketch(context, id + "F22", { "sketchPlane" : qUnion([Q0])});
            skPoint(sketch, "E60.0", {"position": v(-57.6, 70) * mm});
            skLineSegment(sketch, "E61", {"start": v(-57.6, 70) * mm, "end": v(-43.6, 70) * mm, "construction": true});
            skLineSegment(sketch, "E62", {"start": v(-43.6, 70) * mm, "end": v(-28.1, 70) * mm, "construction": true});
            skLineSegment(sketch, "E63", {"start": v(-28.1, 70) * mm, "end": v(-12.6, 70) * mm, "construction": true});
            skLineSegment(sketch, "E64", {"start": v(-28.1, 70) * mm, "end": v(-28.1, 63.5) * mm, "construction": true});
            skLineSegment(sketch, "E65", {"start": v(-28.1, 63.5) * mm, "end": v(-28.1, 32.5) * mm, "construction": true});
            skLineSegment(sketch, "E66", {"start": v(-28.1, 32.5) * mm, "end": v(-43.6, 32.5) * mm, "construction": true});
            skLineSegment(sketch, "E67", {"start": v(-43.6, 32.5) * mm, "end": v(-43.6, 63.5) * mm, "construction": true});
            skLineSegment(sketch, "E68", {"start": v(-28.1, 32.5) * mm, "end": v(-12.6, 32.5) * mm, "construction": true});
            skLineSegment(sketch, "E69", {"start": v(-12.6, 32.5) * mm, "end": v(-12.6, 63.5) * mm, "construction": true});
            skCircle(sketch, "E70", {"center": v(-28.1, 48) * mm, "radius": 11.1 * mm});
            skCircle(sketch, "E71", {"center": v(-43.6, 63.5) * mm, "radius": 1.7 * mm});
            skCircle(sketch, "E72", {"center": v(-12.6, 63.5) * mm, "radius": 1.7 * mm});
            skCircle(sketch, "E73", {"center": v(-12.6, 32.5) * mm, "radius": 1.7 * mm});
            skCircle(sketch, "E74", {"center": v(-43.6, 32.5) * mm, "radius": 1.7 * mm});
            skSolve(sketch);
        }
        {
            var Q0;
            Q0 = qSketchRegion(id + "F22", true);
            extrude(context, id + "F23", {"entities" : qUnion([Q0]), "operationType" : NewBodyOperationType.REMOVE, "oppositeDirection" : true, "depth" : 25 * mm});
        }
        {
            var Q0;
            Q0=makeQuery(id+"F21.opExtrude","SWEPT_FACE",FACE,{"disambiguationData":[OSD([sQuery(id+"F20.wireOp",EDGE,"E56")])]});
            var sketch = newSketch(context, id + "F24", { "sketchPlane" : qUnion([Q0])});
            skLineSegment(sketch, "E75", {"start": v(107.48, 70) * mm, "end": v(97.48, 70) * mm, "construction": true});
            skLineSegment(sketch, "E76", {"start": v(97.48, 70) * mm, "end": v(97.48, 60) * mm, "construction": true});
            skLineSegment(sketch, "E77", {"start": v(107.48, 0) * mm, "end": v(97.48, 0) * mm, "construction": true});
            skLineSegment(sketch, "E78", {"start": v(97.48, 0) * mm, "end": v(97.48, 10) * mm, "construction": true});
            skCircle(sketch, "E79", {"center": v(97.48, 10) * mm, "radius": 2.6 * mm});
            skCircle(sketch, "E80", {"center": v(97.48, 60) * mm, "radius": 2.6 * mm});
            skLineSegment(sketch, "E81", {"start": v(107.48, 0) * mm, "end": v(85.98, 0) * mm, "construction": true});
            skLineSegment(sketch, "E82", {"start": v(85.98, 0) * mm, "end": v(85.98, 10) * mm, "construction": true});
            skCircle(sketch, "E83", {"center": v(85.98, 10) * mm, "radius": 1.7 * mm});
            skLineSegment(sketch, "E84", {"start": v(107.48, 0) * mm, "end": v(56.48, 0) * mm, "construction": true});
            skLineSegment(sketch, "E85", {"start": v(56.48, 0) * mm, "end": v(56.48, 7) * mm, "construction": true});
            skCircle(sketch, "E86", {"center": v(56.48, 7) * mm, "radius": 2 * mm});
            skLineSegment(sketch, "E87", {"start": v(31.48, 0) * mm, "end": v(43.98, 0) * mm, "construction": true});
            skLineSegment(sketch, "E88", {"start": v(43.98, 0) * mm, "end": v(43.98, 19) * mm, "construction": true});
            skCircle(sketch, "E89", {"center": v(43.98, 19) * mm, "radius": 5.75 * mm});
            skLineSegment(sketch, "E90", {"start": v(107.48, 70) * mm, "end": v(85.98, 70) * mm, "construction": true});
            skLineSegment(sketch, "E91", {"start": v(85.98, 70) * mm, "end": v(85.98, 60) * mm, "construction": true});
            skCircle(sketch, "E92", {"center": v(85.98, 60) * mm, "radius": 1.7 * mm});
            skSolve(sketch);
        }
        {
            var Q0;
            Q0 = qSketchRegion(id + "F24", true);
            extrude(context, id + "F25", {"entities" : qUnion([Q0]), "operationType" : NewBodyOperationType.REMOVE, "oppositeDirection" : true, "depth" : 25 * mm});
        }
        {
            var Q0;
            Q0=makeQuery(id+"F21.opExtrude","SWEPT_FACE",FACE,{"disambiguationData":[OSD([sQuery(id+"F20.wireOp",EDGE,"E56")])]});
            var sketch = newSketch(context, id + "F26", { "sketchPlane" : qUnion([Q0])});
            skText(sketch, "E93", { "text": "v0.1 RC1.0\n        B,R", "fontName": "OpenSans-Bold.ttf"});
            const initialGuessF26  = {"E93": [0.03424, 0.0414, 1, 0, 0.01006]};
            skSetInitialGuess(sketch, initialGuessF26);
            skSolve(sketch);
        }
        {
            var Q0;
            Q0 = qSketchRegion(id + "F26", true);
            extrude(context, id + "F27", {"entities" : qUnion([Q0]), "operationType" : NewBodyOperationType.REMOVE, "oppositeDirection" : true, "depth" : .5 * mm});
        }
        {
            var Q0;
            Q0=makeQuery(id+"F27.boolean.opBoolean","COPY",FACE,{"derivedFrom":makeQuery(id+"F27.opExtrude","CAP_FACE",FACE,{"disambiguationData":[OSD([sQuery(id+"F26.wireOp",EDGE,"E93.sketch_text.stroke-0"),sQuery(id+"F26.wireOp",EDGE,"E93.sketch_text.stroke-1"),sQuery(id+"F26.wireOp",EDGE,"E93.sketch_text.stroke-2"),sQuery(id+"F26.wireOp",EDGE,"E93.sketch_text.stroke-3"),sQuery(id+"F26.wireOp",EDGE,"E93.sketch_text.stroke-4"),sQuery(id+"F26.wireOp",EDGE,"E93.sketch_text.stroke-5"),sQuery(id+"F26.wireOp",EDGE,"E93.sketch_text.stroke-6"),sQuery(id+"F26.wireOp",EDGE,"E93.sketch_text.stroke-7"),sQuery(id+"F26.wireOp",EDGE,"E93.sketch_text.stroke-8"),sQuery(id+"F26.wireOp",EDGE,"E93.sketch_text.stroke-9")])],"isStart":false})});
            var Q1;
            Q1=makeQuery(id+"F27.boolean.opBoolean","COPY",FACE,{"derivedFrom":makeQuery(id+"F27.opExtrude","CAP_FACE",FACE,{"disambiguationData":[OSD([sQuery(id+"F26.wireOp",EDGE,"E93.sketch_text.stroke-10"),sQuery(id+"F26.wireOp",EDGE,"E93.sketch_text.stroke-11"),sQuery(id+"F26.wireOp",EDGE,"E93.sketch_text.stroke-12"),sQuery(id+"F26.wireOp",EDGE,"E93.sketch_text.stroke-13"),sQuery(id+"F26.wireOp",EDGE,"E93.sketch_text.stroke-14"),sQuery(id+"F26.wireOp",EDGE,"E93.sketch_text.stroke-15"),sQuery(id+"F26.wireOp",EDGE,"E93.sketch_text.stroke-16"),sQuery(id+"F26.wireOp",EDGE,"E93.sketch_text.stroke-17"),sQuery(id+"F26.wireOp",EDGE,"E93.sketch_text.stroke-18"),sQuery(id+"F26.wireOp",EDGE,"E93.sketch_text.stroke-19"),sQuery(id+"F26.wireOp",EDGE,"E93.sketch_text.stroke-20"),sQuery(id+"F26.wireOp",EDGE,"E93.sketch_text.stroke-21"),sQuery(id+"F26.wireOp",EDGE,"E93.sketch_text.stroke-22"),sQuery(id+"F26.wireOp",EDGE,"E93.sketch_text.stroke-23"),sQuery(id+"F26.wireOp",EDGE,"E93.sketch_text.stroke-24"),sQuery(id+"F26.wireOp",EDGE,"E93.sketch_text.stroke-25")])],"isStart":false})});
            var Q2;
            Q2=makeQuery(id+"F27.boolean.opBoolean","COPY",FACE,{"derivedFrom":makeQuery(id+"F27.opExtrude","CAP_FACE",FACE,{"disambiguationData":[OSD([sQuery(id+"F26.wireOp",EDGE,"E93.sketch_text.stroke-34"),sQuery(id+"F26.wireOp",EDGE,"E93.sketch_text.stroke-35"),sQuery(id+"F26.wireOp",EDGE,"E93.sketch_text.stroke-36"),sQuery(id+"F26.wireOp",EDGE,"E93.sketch_text.stroke-37"),sQuery(id+"F26.wireOp",EDGE,"E93.sketch_text.stroke-38"),sQuery(id+"F26.wireOp",EDGE,"E93.sketch_text.stroke-39"),sQuery(id+"F26.wireOp",EDGE,"E93.sketch_text.stroke-40"),sQuery(id+"F26.wireOp",EDGE,"E93.sketch_text.stroke-41"),sQuery(id+"F26.wireOp",EDGE,"E93.sketch_text.stroke-42"),sQuery(id+"F26.wireOp",EDGE,"E93.sketch_text.stroke-43")])],"isStart":false})});
            var Q3;
            Q3=makeQuery(id+"F27.boolean.opBoolean","COPY",FACE,{"derivedFrom":makeQuery(id+"F27.opExtrude","CAP_FACE",FACE,{"disambiguationData":[OSD([sQuery(id+"F26.wireOp",EDGE,"E93.sketch_text.stroke-26"),sQuery(id+"F26.wireOp",EDGE,"E93.sketch_text.stroke-27"),sQuery(id+"F26.wireOp",EDGE,"E93.sketch_text.stroke-28"),sQuery(id+"F26.wireOp",EDGE,"E93.sketch_text.stroke-29"),sQuery(id+"F26.wireOp",EDGE,"E93.sketch_text.stroke-30"),sQuery(id+"F26.wireOp",EDGE,"E93.sketch_text.stroke-31"),sQuery(id+"F26.wireOp",EDGE,"E93.sketch_text.stroke-32"),sQuery(id+"F26.wireOp",EDGE,"E93.sketch_text.stroke-33")])],"isStart":false})});
            var Q4;
            Q4=makeQuery(id+"F27.boolean.opBoolean","COPY",FACE,{"derivedFrom":makeQuery(id+"F27.opExtrude","CAP_FACE",FACE,{"disambiguationData":[OSD([sQuery(id+"F26.wireOp",EDGE,"E93.sketch_text.stroke-44"),sQuery(id+"F26.wireOp",EDGE,"E93.sketch_text.stroke-45"),sQuery(id+"F26.wireOp",EDGE,"E93.sketch_text.stroke-46"),sQuery(id+"F26.wireOp",EDGE,"E93.sketch_text.stroke-47"),sQuery(id+"F26.wireOp",EDGE,"E93.sketch_text.stroke-48"),sQuery(id+"F26.wireOp",EDGE,"E93.sketch_text.stroke-49"),sQuery(id+"F26.wireOp",EDGE,"E93.sketch_text.stroke-50"),sQuery(id+"F26.wireOp",EDGE,"E93.sketch_text.stroke-51"),sQuery(id+"F26.wireOp",EDGE,"E93.sketch_text.stroke-52"),sQuery(id+"F26.wireOp",EDGE,"E93.sketch_text.stroke-53"),sQuery(id+"F26.wireOp",EDGE,"E93.sketch_text.stroke-54"),sQuery(id+"F26.wireOp",EDGE,"E93.sketch_text.stroke-55"),sQuery(id+"F26.wireOp",EDGE,"E93.sketch_text.stroke-56"),sQuery(id+"F26.wireOp",EDGE,"E93.sketch_text.stroke-57"),sQuery(id+"F26.wireOp",EDGE,"E93.sketch_text.stroke-58"),sQuery(id+"F26.wireOp",EDGE,"E93.sketch_text.stroke-59"),sQuery(id+"F26.wireOp",EDGE,"E93.sketch_text.stroke-60"),sQuery(id+"F26.wireOp",EDGE,"E93.sketch_text.stroke-61"),sQuery(id+"F26.wireOp",EDGE,"E93.sketch_text.stroke-62")])],"isStart":false})});
            var Q5;
            Q5=makeQuery(id+"F27.boolean.opBoolean","COPY",FACE,{"derivedFrom":makeQuery(id+"F27.opExtrude","CAP_FACE",FACE,{"disambiguationData":[OSD([sQuery(id+"F26.wireOp",EDGE,"E93.sketch_text.stroke-63"),sQuery(id+"F26.wireOp",EDGE,"E93.sketch_text.stroke-64"),sQuery(id+"F26.wireOp",EDGE,"E93.sketch_text.stroke-65"),sQuery(id+"F26.wireOp",EDGE,"E93.sketch_text.stroke-66"),sQuery(id+"F26.wireOp",EDGE,"E93.sketch_text.stroke-67"),sQuery(id+"F26.wireOp",EDGE,"E93.sketch_text.stroke-68"),sQuery(id+"F26.wireOp",EDGE,"E93.sketch_text.stroke-69"),sQuery(id+"F26.wireOp",EDGE,"E93.sketch_text.stroke-70"),sQuery(id+"F26.wireOp",EDGE,"E93.sketch_text.stroke-71"),sQuery(id+"F26.wireOp",EDGE,"E93.sketch_text.stroke-72"),sQuery(id+"F26.wireOp",EDGE,"E93.sketch_text.stroke-73"),sQuery(id+"F26.wireOp",EDGE,"E93.sketch_text.stroke-74"),sQuery(id+"F26.wireOp",EDGE,"E93.sketch_text.stroke-75"),sQuery(id+"F26.wireOp",EDGE,"E93.sketch_text.stroke-76"),sQuery(id+"F26.wireOp",EDGE,"E93.sketch_text.stroke-77")])],"isStart":false})});
            var Q6;
            Q6=makeQuery(id+"F27.boolean.opBoolean","COPY",FACE,{"derivedFrom":makeQuery(id+"F27.opExtrude","CAP_FACE",FACE,{"disambiguationData":[OSD([sQuery(id+"F26.wireOp",EDGE,"E93.sketch_text.stroke-78"),sQuery(id+"F26.wireOp",EDGE,"E93.sketch_text.stroke-79"),sQuery(id+"F26.wireOp",EDGE,"E93.sketch_text.stroke-80"),sQuery(id+"F26.wireOp",EDGE,"E93.sketch_text.stroke-81"),sQuery(id+"F26.wireOp",EDGE,"E93.sketch_text.stroke-82"),sQuery(id+"F26.wireOp",EDGE,"E93.sketch_text.stroke-83"),sQuery(id+"F26.wireOp",EDGE,"E93.sketch_text.stroke-84"),sQuery(id+"F26.wireOp",EDGE,"E93.sketch_text.stroke-85"),sQuery(id+"F26.wireOp",EDGE,"E93.sketch_text.stroke-86"),sQuery(id+"F26.wireOp",EDGE,"E93.sketch_text.stroke-87")])],"isStart":false})});
            var Q7;
            Q7=makeQuery(id+"F27.boolean.opBoolean","COPY",FACE,{"derivedFrom":makeQuery(id+"F27.opExtrude","CAP_FACE",FACE,{"disambiguationData":[OSD([sQuery(id+"F26.wireOp",EDGE,"E93.sketch_text.stroke-96"),sQuery(id+"F26.wireOp",EDGE,"E93.sketch_text.stroke-97"),sQuery(id+"F26.wireOp",EDGE,"E93.sketch_text.stroke-98"),sQuery(id+"F26.wireOp",EDGE,"E93.sketch_text.stroke-99"),sQuery(id+"F26.wireOp",EDGE,"E93.sketch_text.stroke-100"),sQuery(id+"F26.wireOp",EDGE,"E93.sketch_text.stroke-101"),sQuery(id+"F26.wireOp",EDGE,"E93.sketch_text.stroke-102"),sQuery(id+"F26.wireOp",EDGE,"E93.sketch_text.stroke-103"),sQuery(id+"F26.wireOp",EDGE,"E93.sketch_text.stroke-104"),sQuery(id+"F26.wireOp",EDGE,"E93.sketch_text.stroke-105"),sQuery(id+"F26.wireOp",EDGE,"E93.sketch_text.stroke-106"),sQuery(id+"F26.wireOp",EDGE,"E93.sketch_text.stroke-107"),sQuery(id+"F26.wireOp",EDGE,"E93.sketch_text.stroke-108"),sQuery(id+"F26.wireOp",EDGE,"E93.sketch_text.stroke-109"),sQuery(id+"F26.wireOp",EDGE,"E93.sketch_text.stroke-110"),sQuery(id+"F26.wireOp",EDGE,"E93.sketch_text.stroke-111")])],"isStart":false})});
            var Q8;
            Q8=makeQuery(id+"F27.boolean.opBoolean","COPY",FACE,{"derivedFrom":makeQuery(id+"F27.opExtrude","CAP_FACE",FACE,{"disambiguationData":[OSD([sQuery(id+"F26.wireOp",EDGE,"E93.sketch_text.stroke-88"),sQuery(id+"F26.wireOp",EDGE,"E93.sketch_text.stroke-89"),sQuery(id+"F26.wireOp",EDGE,"E93.sketch_text.stroke-90"),sQuery(id+"F26.wireOp",EDGE,"E93.sketch_text.stroke-91"),sQuery(id+"F26.wireOp",EDGE,"E93.sketch_text.stroke-92"),sQuery(id+"F26.wireOp",EDGE,"E93.sketch_text.stroke-93"),sQuery(id+"F26.wireOp",EDGE,"E93.sketch_text.stroke-94"),sQuery(id+"F26.wireOp",EDGE,"E93.sketch_text.stroke-95")])],"isStart":false})});
            var Q9;
            Q9=makeQuery(id+"F27.boolean.opBoolean","COPY",FACE,{"derivedFrom":makeQuery(id+"F27.opExtrude","CAP_FACE",FACE,{"disambiguationData":[OSD([sQuery(id+"F26.wireOp",EDGE,"E93.sketch_text.stroke-112"),sQuery(id+"F26.wireOp",EDGE,"E93.sketch_text.stroke-113"),sQuery(id+"F26.wireOp",EDGE,"E93.sketch_text.stroke-114"),sQuery(id+"F26.wireOp",EDGE,"E93.sketch_text.stroke-115"),sQuery(id+"F26.wireOp",EDGE,"E93.sketch_text.stroke-116"),sQuery(id+"F26.wireOp",EDGE,"E93.sketch_text.stroke-117"),sQuery(id+"F26.wireOp",EDGE,"E93.sketch_text.stroke-118"),sQuery(id+"F26.wireOp",EDGE,"E93.sketch_text.stroke-119"),sQuery(id+"F26.wireOp",EDGE,"E93.sketch_text.stroke-120"),sQuery(id+"F26.wireOp",EDGE,"E93.sketch_text.stroke-121"),sQuery(id+"F26.wireOp",EDGE,"E93.sketch_text.stroke-122"),sQuery(id+"F26.wireOp",EDGE,"E93.sketch_text.stroke-123"),sQuery(id+"F26.wireOp",EDGE,"E93.sketch_text.stroke-124"),sQuery(id+"F26.wireOp",EDGE,"E93.sketch_text.stroke-125"),sQuery(id+"F26.wireOp",EDGE,"E93.sketch_text.stroke-126"),sQuery(id+"F26.wireOp",EDGE,"E93.sketch_text.stroke-127"),sQuery(id+"F26.wireOp",EDGE,"E93.sketch_text.stroke-128"),sQuery(id+"F26.wireOp",EDGE,"E93.sketch_text.stroke-129"),sQuery(id+"F26.wireOp",EDGE,"E93.sketch_text.stroke-130"),sQuery(id+"F26.wireOp",EDGE,"E93.sketch_text.stroke-131"),sQuery(id+"F26.wireOp",EDGE,"E93.sketch_text.stroke-132"),sQuery(id+"F26.wireOp",EDGE,"E93.sketch_text.stroke-133"),sQuery(id+"F26.wireOp",EDGE,"E93.sketch_text.stroke-134"),sQuery(id+"F26.wireOp",EDGE,"E93.sketch_text.stroke-135"),sQuery(id+"F26.wireOp",EDGE,"E93.sketch_text.stroke-136")])],"isStart":false})});
            var Q10;
            Q10=makeQuery(id+"F27.boolean.opBoolean","COPY",FACE,{"derivedFrom":makeQuery(id+"F27.opExtrude","CAP_FACE",FACE,{"disambiguationData":[OSD([sQuery(id+"F26.wireOp",EDGE,"E93.sketch_text.stroke-137"),sQuery(id+"F26.wireOp",EDGE,"E93.sketch_text.stroke-138"),sQuery(id+"F26.wireOp",EDGE,"E93.sketch_text.stroke-139"),sQuery(id+"F26.wireOp",EDGE,"E93.sketch_text.stroke-140"),sQuery(id+"F26.wireOp",EDGE,"E93.sketch_text.stroke-141")])],"isStart":false})});
            var Q11;
            Q11=makeQuery(id+"F27.boolean.opBoolean","COPY",FACE,{"derivedFrom":makeQuery(id+"F27.opExtrude","CAP_FACE",FACE,{"disambiguationData":[OSD([sQuery(id+"F26.wireOp",EDGE,"E93.sketch_text.stroke-142"),sQuery(id+"F26.wireOp",EDGE,"E93.sketch_text.stroke-143"),sQuery(id+"F26.wireOp",EDGE,"E93.sketch_text.stroke-144"),sQuery(id+"F26.wireOp",EDGE,"E93.sketch_text.stroke-145"),sQuery(id+"F26.wireOp",EDGE,"E93.sketch_text.stroke-146"),sQuery(id+"F26.wireOp",EDGE,"E93.sketch_text.stroke-147"),sQuery(id+"F26.wireOp",EDGE,"E93.sketch_text.stroke-148"),sQuery(id+"F26.wireOp",EDGE,"E93.sketch_text.stroke-149"),sQuery(id+"F26.wireOp",EDGE,"E93.sketch_text.stroke-150"),sQuery(id+"F26.wireOp",EDGE,"E93.sketch_text.stroke-151"),sQuery(id+"F26.wireOp",EDGE,"E93.sketch_text.stroke-152"),sQuery(id+"F26.wireOp",EDGE,"E93.sketch_text.stroke-153"),sQuery(id+"F26.wireOp",EDGE,"E93.sketch_text.stroke-154"),sQuery(id+"F26.wireOp",EDGE,"E93.sketch_text.stroke-155"),sQuery(id+"F26.wireOp",EDGE,"E93.sketch_text.stroke-156"),sQuery(id+"F26.wireOp",EDGE,"E93.sketch_text.stroke-157"),sQuery(id+"F26.wireOp",EDGE,"E93.sketch_text.stroke-158"),sQuery(id+"F26.wireOp",EDGE,"E93.sketch_text.stroke-159"),sQuery(id+"F26.wireOp",EDGE,"E93.sketch_text.stroke-160")])],"isStart":false})});
            chamfer(context, id + "F28", {"entities" : qUnion([Q0, Q1, Q2, Q3, Q4, Q5, Q6, Q7, Q8, Q9, Q10, Q11]), "width" : .5 * mm, "tangentPropagation" : true});
        }
        {
            var Q0;
            Q0=qCreatedBy(makeId("Top.planeOp"),FACE);
            var sketch = newSketch(context, id + "F29", { "sketchPlane" : qUnion([Q0])});
            skLineSegment(sketch, "E94", {"start": v(-18.1, -43.44) * mm, "end": v(-11.7, -43.44) * mm});
            skLineSegment(sketch, "E95", {"start": v(-11.7, -43.44) * mm, "end": v(-11.7, -119.44) * mm});
            skLineSegment(sketch, "E96", {"start": v(-11.7, -119.44) * mm, "end": v(-62.7, -119.44) * mm});
            skLineSegment(sketch, "E97", {"start": v(-62.7, -119.44) * mm, "end": v(-62.7, -113.04) * mm});
            skLineSegment(sketch, "E98", {"start": v(-62.7, -113.04) * mm, "end": v(-18.1, -113.04) * mm});
            skLineSegment(sketch, "E99", {"start": v(-18.1, -113.04) * mm, "end": v(-18.1, -43.44) * mm});
            skSolve(sketch);
        }
        {
            var Q0;
            Q0 = qSketchRegion(id + "F29", true);
            extrude(context, id + "F30", {"entities" : qUnion([Q0]), "depth" : 70 * mm});
        }
        {
            var Q0;
            Q0=makeQuery(id+"F30.opExtrude","SWEPT_FACE",FACE,{"disambiguationData":[OSD([sQuery(id+"F29.wireOp",EDGE,"E96")])]});
            var sketch = newSketch(context, id + "F31", { "sketchPlane" : qUnion([Q0])});
            skLineSegment(sketch, "E100", {"start": v(-11.7, 70) * mm, "end": v(-31.7, 70) * mm, "construction": true});
            skLineSegment(sketch, "E101", {"start": v(-31.7, 70) * mm, "end": v(-31.7, 50) * mm, "construction": true});
            skCircle(sketch, "E102", {"center": v(-31.7, 50) * mm, "radius": 4.05 * mm});
            skLineSegment(sketch, "E103", {"start": v(-11.7, 0) * mm, "end": v(-29.7, 0) * mm, "construction": true});
            skLineSegment(sketch, "E104", {"start": v(-29.7, 0) * mm, "end": v(-29.7, 5) * mm});
            skCircle(sketch, "E105", {"center": v(-29.7, 5) * mm, "radius": 1.7 * mm});
            skSolve(sketch);
        }
        {
            var Q0;
            Q0 = qSketchRegion(id + "F31", true);
            extrude(context, id + "F32", {"entities" : qUnion([Q0]), "operationType" : NewBodyOperationType.REMOVE, "oppositeDirection" : true, "depth" : 25 * mm});
        }
        {
            var Q0;
            Q0=makeQuery(id+"F30.opExtrude","SWEPT_FACE",FACE,{"disambiguationData":[OSD([sQuery(id+"F29.wireOp",EDGE,"E99")])]});
            var sketch = newSketch(context, id + "F33", { "sketchPlane" : qUnion([Q0])});
            skLineSegment(sketch, "E106", {"start": v(43.44, 70) * mm, "end": v(53.44, 70) * mm, "construction": true});
            skLineSegment(sketch, "E107", {"start": v(53.44, 70) * mm, "end": v(53.44, 60) * mm, "construction": true});
            skLineSegment(sketch, "E108", {"start": v(43.44, 0) * mm, "end": v(53.44, 0) * mm, "construction": true});
            skLineSegment(sketch, "E109", {"start": v(53.44, 0) * mm, "end": v(53.44, 10) * mm, "construction": true});
            skCircle(sketch, "E110", {"center": v(53.44, 60) * mm, "radius": 2.6 * mm});
            skCircle(sketch, "E111", {"center": v(53.44, 10) * mm, "radius": 2.6 * mm});
            skLineSegment(sketch, "E112", {"start": v(43.44, 70) * mm, "end": v(64.94, 70) * mm, "construction": true});
            skLineSegment(sketch, "E113", {"start": v(64.94, 70) * mm, "end": v(64.94, 60) * mm, "construction": true});
            skCircle(sketch, "E114", {"center": v(64.94, 60) * mm, "radius": 1.7 * mm});
            skLineSegment(sketch, "E115", {"start": v(43.44, 70) * mm, "end": v(103.44, 70) * mm, "construction": true});
            skLineSegment(sketch, "E116", {"start": v(103.44, 70) * mm, "end": v(103.44, 65) * mm, "construction": true});
            skCircle(sketch, "E117", {"center": v(103.44, 65) * mm, "radius": 1.7 * mm});
            skLineSegment(sketch, "E118", {"start": v(43.44, 0) * mm, "end": v(64.94, 0) * mm, "construction": true});
            skLineSegment(sketch, "E119", {"start": v(64.94, 0) * mm, "end": v(64.94, 10) * mm, "construction": true});
            skCircle(sketch, "E120", {"center": v(64.94, 10) * mm, "radius": 1.7 * mm});
            skLineSegment(sketch, "E121", {"start": v(43.44, 0) * mm, "end": v(94.44, 0) * mm, "construction": true});
            skLineSegment(sketch, "E122", {"start": v(94.44, 0) * mm, "end": v(94.44, 7) * mm, "construction": true});
            skCircle(sketch, "E123", {"center": v(94.44, 7) * mm, "radius": 2 * mm});
            skSolve(sketch);
        }
        {
            var Q0;
            Q0 = qSketchRegion(id + "F33", true);
            extrude(context, id + "F34", {"entities" : qUnion([Q0]), "operationType" : NewBodyOperationType.REMOVE, "oppositeDirection" : true, "depth" : 25 * mm});
        }
        {
            var Q0;
            Q0=makeQuery(id+"F30.opExtrude","SWEPT_FACE",FACE,{"disambiguationData":[OSD([sQuery(id+"F29.wireOp",EDGE,"E95")])]});
            var sketch = newSketch(context, id + "F35", { "sketchPlane" : qUnion([Q0])});
            skText(sketch, "E124", { "text": "v0.1 RC1.0\nF,L", "fontName": "OpenSans-Bold.ttf"});
            const initialGuessF35  = {"E124": [-0.11621, 0.04284, 1, 0, 0.01006]};
            skSetInitialGuess(sketch, initialGuessF35);
            skSolve(sketch);
        }
        {
            var Q0;
            Q0 = qSketchRegion(id + "F35", true);
            extrude(context, id + "F36", {"entities" : qUnion([Q0]), "operationType" : NewBodyOperationType.REMOVE, "oppositeDirection" : true, "depth" : .5 * mm});
        }
        {
            var Q0;
            Q0=makeQuery(id+"F36.boolean.opBoolean","COPY",FACE,{"derivedFrom":makeQuery(id+"F36.opExtrude","CAP_FACE",FACE,{"disambiguationData":[OSD([sQuery(id+"F35.wireOp",EDGE,"E124.sketch_text.stroke-0"),sQuery(id+"F35.wireOp",EDGE,"E124.sketch_text.stroke-1"),sQuery(id+"F35.wireOp",EDGE,"E124.sketch_text.stroke-2"),sQuery(id+"F35.wireOp",EDGE,"E124.sketch_text.stroke-3"),sQuery(id+"F35.wireOp",EDGE,"E124.sketch_text.stroke-4"),sQuery(id+"F35.wireOp",EDGE,"E124.sketch_text.stroke-5"),sQuery(id+"F35.wireOp",EDGE,"E124.sketch_text.stroke-6"),sQuery(id+"F35.wireOp",EDGE,"E124.sketch_text.stroke-7"),sQuery(id+"F35.wireOp",EDGE,"E124.sketch_text.stroke-8"),sQuery(id+"F35.wireOp",EDGE,"E124.sketch_text.stroke-9")])],"isStart":false})});
            var Q1;
            Q1=makeQuery(id+"F36.boolean.opBoolean","COPY",FACE,{"derivedFrom":makeQuery(id+"F36.opExtrude","CAP_FACE",FACE,{"disambiguationData":[OSD([sQuery(id+"F35.wireOp",EDGE,"E124.sketch_text.stroke-10"),sQuery(id+"F35.wireOp",EDGE,"E124.sketch_text.stroke-11"),sQuery(id+"F35.wireOp",EDGE,"E124.sketch_text.stroke-12"),sQuery(id+"F35.wireOp",EDGE,"E124.sketch_text.stroke-13"),sQuery(id+"F35.wireOp",EDGE,"E124.sketch_text.stroke-14"),sQuery(id+"F35.wireOp",EDGE,"E124.sketch_text.stroke-15"),sQuery(id+"F35.wireOp",EDGE,"E124.sketch_text.stroke-16"),sQuery(id+"F35.wireOp",EDGE,"E124.sketch_text.stroke-17"),sQuery(id+"F35.wireOp",EDGE,"E124.sketch_text.stroke-18"),sQuery(id+"F35.wireOp",EDGE,"E124.sketch_text.stroke-19"),sQuery(id+"F35.wireOp",EDGE,"E124.sketch_text.stroke-20"),sQuery(id+"F35.wireOp",EDGE,"E124.sketch_text.stroke-21"),sQuery(id+"F35.wireOp",EDGE,"E124.sketch_text.stroke-22"),sQuery(id+"F35.wireOp",EDGE,"E124.sketch_text.stroke-23"),sQuery(id+"F35.wireOp",EDGE,"E124.sketch_text.stroke-24"),sQuery(id+"F35.wireOp",EDGE,"E124.sketch_text.stroke-25")])],"isStart":false})});
            var Q2;
            Q2=makeQuery(id+"F36.boolean.opBoolean","COPY",FACE,{"derivedFrom":makeQuery(id+"F36.opExtrude","CAP_FACE",FACE,{"disambiguationData":[OSD([sQuery(id+"F35.wireOp",EDGE,"E124.sketch_text.stroke-26"),sQuery(id+"F35.wireOp",EDGE,"E124.sketch_text.stroke-27"),sQuery(id+"F35.wireOp",EDGE,"E124.sketch_text.stroke-28"),sQuery(id+"F35.wireOp",EDGE,"E124.sketch_text.stroke-29"),sQuery(id+"F35.wireOp",EDGE,"E124.sketch_text.stroke-30"),sQuery(id+"F35.wireOp",EDGE,"E124.sketch_text.stroke-31"),sQuery(id+"F35.wireOp",EDGE,"E124.sketch_text.stroke-32"),sQuery(id+"F35.wireOp",EDGE,"E124.sketch_text.stroke-33")])],"isStart":false})});
            var Q3;
            Q3=makeQuery(id+"F36.boolean.opBoolean","COPY",FACE,{"derivedFrom":makeQuery(id+"F36.opExtrude","CAP_FACE",FACE,{"disambiguationData":[OSD([sQuery(id+"F35.wireOp",EDGE,"E124.sketch_text.stroke-34"),sQuery(id+"F35.wireOp",EDGE,"E124.sketch_text.stroke-35"),sQuery(id+"F35.wireOp",EDGE,"E124.sketch_text.stroke-36"),sQuery(id+"F35.wireOp",EDGE,"E124.sketch_text.stroke-37"),sQuery(id+"F35.wireOp",EDGE,"E124.sketch_text.stroke-38"),sQuery(id+"F35.wireOp",EDGE,"E124.sketch_text.stroke-39"),sQuery(id+"F35.wireOp",EDGE,"E124.sketch_text.stroke-40"),sQuery(id+"F35.wireOp",EDGE,"E124.sketch_text.stroke-41"),sQuery(id+"F35.wireOp",EDGE,"E124.sketch_text.stroke-42"),sQuery(id+"F35.wireOp",EDGE,"E124.sketch_text.stroke-43")])],"isStart":false})});
            var Q4;
            Q4=makeQuery(id+"F36.boolean.opBoolean","COPY",FACE,{"derivedFrom":makeQuery(id+"F36.opExtrude","CAP_FACE",FACE,{"disambiguationData":[OSD([sQuery(id+"F35.wireOp",EDGE,"E124.sketch_text.stroke-44"),sQuery(id+"F35.wireOp",EDGE,"E124.sketch_text.stroke-45"),sQuery(id+"F35.wireOp",EDGE,"E124.sketch_text.stroke-46"),sQuery(id+"F35.wireOp",EDGE,"E124.sketch_text.stroke-47"),sQuery(id+"F35.wireOp",EDGE,"E124.sketch_text.stroke-48"),sQuery(id+"F35.wireOp",EDGE,"E124.sketch_text.stroke-49"),sQuery(id+"F35.wireOp",EDGE,"E124.sketch_text.stroke-50"),sQuery(id+"F35.wireOp",EDGE,"E124.sketch_text.stroke-51"),sQuery(id+"F35.wireOp",EDGE,"E124.sketch_text.stroke-52"),sQuery(id+"F35.wireOp",EDGE,"E124.sketch_text.stroke-53"),sQuery(id+"F35.wireOp",EDGE,"E124.sketch_text.stroke-54"),sQuery(id+"F35.wireOp",EDGE,"E124.sketch_text.stroke-55"),sQuery(id+"F35.wireOp",EDGE,"E124.sketch_text.stroke-56"),sQuery(id+"F35.wireOp",EDGE,"E124.sketch_text.stroke-57"),sQuery(id+"F35.wireOp",EDGE,"E124.sketch_text.stroke-58"),sQuery(id+"F35.wireOp",EDGE,"E124.sketch_text.stroke-59"),sQuery(id+"F35.wireOp",EDGE,"E124.sketch_text.stroke-60"),sQuery(id+"F35.wireOp",EDGE,"E124.sketch_text.stroke-61"),sQuery(id+"F35.wireOp",EDGE,"E124.sketch_text.stroke-62")])],"isStart":false})});
            var Q5;
            Q5=makeQuery(id+"F36.boolean.opBoolean","COPY",FACE,{"derivedFrom":makeQuery(id+"F36.opExtrude","CAP_FACE",FACE,{"disambiguationData":[OSD([sQuery(id+"F35.wireOp",EDGE,"E124.sketch_text.stroke-63"),sQuery(id+"F35.wireOp",EDGE,"E124.sketch_text.stroke-64"),sQuery(id+"F35.wireOp",EDGE,"E124.sketch_text.stroke-65"),sQuery(id+"F35.wireOp",EDGE,"E124.sketch_text.stroke-66"),sQuery(id+"F35.wireOp",EDGE,"E124.sketch_text.stroke-67"),sQuery(id+"F35.wireOp",EDGE,"E124.sketch_text.stroke-68"),sQuery(id+"F35.wireOp",EDGE,"E124.sketch_text.stroke-69"),sQuery(id+"F35.wireOp",EDGE,"E124.sketch_text.stroke-70"),sQuery(id+"F35.wireOp",EDGE,"E124.sketch_text.stroke-71"),sQuery(id+"F35.wireOp",EDGE,"E124.sketch_text.stroke-72"),sQuery(id+"F35.wireOp",EDGE,"E124.sketch_text.stroke-73"),sQuery(id+"F35.wireOp",EDGE,"E124.sketch_text.stroke-74"),sQuery(id+"F35.wireOp",EDGE,"E124.sketch_text.stroke-75"),sQuery(id+"F35.wireOp",EDGE,"E124.sketch_text.stroke-76"),sQuery(id+"F35.wireOp",EDGE,"E124.sketch_text.stroke-77")])],"isStart":false})});
            var Q6;
            Q6=makeQuery(id+"F36.boolean.opBoolean","COPY",FACE,{"derivedFrom":makeQuery(id+"F36.opExtrude","CAP_FACE",FACE,{"disambiguationData":[OSD([sQuery(id+"F35.wireOp",EDGE,"E124.sketch_text.stroke-78"),sQuery(id+"F35.wireOp",EDGE,"E124.sketch_text.stroke-79"),sQuery(id+"F35.wireOp",EDGE,"E124.sketch_text.stroke-80"),sQuery(id+"F35.wireOp",EDGE,"E124.sketch_text.stroke-81"),sQuery(id+"F35.wireOp",EDGE,"E124.sketch_text.stroke-82"),sQuery(id+"F35.wireOp",EDGE,"E124.sketch_text.stroke-83"),sQuery(id+"F35.wireOp",EDGE,"E124.sketch_text.stroke-84"),sQuery(id+"F35.wireOp",EDGE,"E124.sketch_text.stroke-85"),sQuery(id+"F35.wireOp",EDGE,"E124.sketch_text.stroke-86"),sQuery(id+"F35.wireOp",EDGE,"E124.sketch_text.stroke-87")])],"isStart":false})});
            var Q7;
            Q7=makeQuery(id+"F36.boolean.opBoolean","COPY",FACE,{"derivedFrom":makeQuery(id+"F36.opExtrude","CAP_FACE",FACE,{"disambiguationData":[OSD([sQuery(id+"F35.wireOp",EDGE,"E124.sketch_text.stroke-96"),sQuery(id+"F35.wireOp",EDGE,"E124.sketch_text.stroke-97"),sQuery(id+"F35.wireOp",EDGE,"E124.sketch_text.stroke-98"),sQuery(id+"F35.wireOp",EDGE,"E124.sketch_text.stroke-99"),sQuery(id+"F35.wireOp",EDGE,"E124.sketch_text.stroke-100"),sQuery(id+"F35.wireOp",EDGE,"E124.sketch_text.stroke-101"),sQuery(id+"F35.wireOp",EDGE,"E124.sketch_text.stroke-102"),sQuery(id+"F35.wireOp",EDGE,"E124.sketch_text.stroke-103"),sQuery(id+"F35.wireOp",EDGE,"E124.sketch_text.stroke-104"),sQuery(id+"F35.wireOp",EDGE,"E124.sketch_text.stroke-105"),sQuery(id+"F35.wireOp",EDGE,"E124.sketch_text.stroke-106"),sQuery(id+"F35.wireOp",EDGE,"E124.sketch_text.stroke-107"),sQuery(id+"F35.wireOp",EDGE,"E124.sketch_text.stroke-108"),sQuery(id+"F35.wireOp",EDGE,"E124.sketch_text.stroke-109"),sQuery(id+"F35.wireOp",EDGE,"E124.sketch_text.stroke-110"),sQuery(id+"F35.wireOp",EDGE,"E124.sketch_text.stroke-111")])],"isStart":false})});
            var Q8;
            Q8=makeQuery(id+"F36.boolean.opBoolean","COPY",FACE,{"derivedFrom":makeQuery(id+"F36.opExtrude","CAP_FACE",FACE,{"disambiguationData":[OSD([sQuery(id+"F35.wireOp",EDGE,"E124.sketch_text.stroke-88"),sQuery(id+"F35.wireOp",EDGE,"E124.sketch_text.stroke-89"),sQuery(id+"F35.wireOp",EDGE,"E124.sketch_text.stroke-90"),sQuery(id+"F35.wireOp",EDGE,"E124.sketch_text.stroke-91"),sQuery(id+"F35.wireOp",EDGE,"E124.sketch_text.stroke-92"),sQuery(id+"F35.wireOp",EDGE,"E124.sketch_text.stroke-93"),sQuery(id+"F35.wireOp",EDGE,"E124.sketch_text.stroke-94"),sQuery(id+"F35.wireOp",EDGE,"E124.sketch_text.stroke-95")])],"isStart":false})});
            var Q9;
            Q9=makeQuery(id+"F36.boolean.opBoolean","COPY",FACE,{"derivedFrom":makeQuery(id+"F36.opExtrude","CAP_FACE",FACE,{"disambiguationData":[OSD([sQuery(id+"F35.wireOp",EDGE,"E124.sketch_text.stroke-112"),sQuery(id+"F35.wireOp",EDGE,"E124.sketch_text.stroke-113"),sQuery(id+"F35.wireOp",EDGE,"E124.sketch_text.stroke-114"),sQuery(id+"F35.wireOp",EDGE,"E124.sketch_text.stroke-115"),sQuery(id+"F35.wireOp",EDGE,"E124.sketch_text.stroke-116"),sQuery(id+"F35.wireOp",EDGE,"E124.sketch_text.stroke-117"),sQuery(id+"F35.wireOp",EDGE,"E124.sketch_text.stroke-118"),sQuery(id+"F35.wireOp",EDGE,"E124.sketch_text.stroke-119"),sQuery(id+"F35.wireOp",EDGE,"E124.sketch_text.stroke-120"),sQuery(id+"F35.wireOp",EDGE,"E124.sketch_text.stroke-121")])],"isStart":false})});
            var Q10;
            Q10=makeQuery(id+"F36.boolean.opBoolean","COPY",FACE,{"derivedFrom":makeQuery(id+"F36.opExtrude","CAP_FACE",FACE,{"disambiguationData":[OSD([sQuery(id+"F35.wireOp",EDGE,"E124.sketch_text.stroke-122"),sQuery(id+"F35.wireOp",EDGE,"E124.sketch_text.stroke-123"),sQuery(id+"F35.wireOp",EDGE,"E124.sketch_text.stroke-124"),sQuery(id+"F35.wireOp",EDGE,"E124.sketch_text.stroke-125"),sQuery(id+"F35.wireOp",EDGE,"E124.sketch_text.stroke-126")])],"isStart":false})});
            var Q11;
            Q11=makeQuery(id+"F36.boolean.opBoolean","COPY",FACE,{"derivedFrom":makeQuery(id+"F36.opExtrude","CAP_FACE",FACE,{"disambiguationData":[OSD([sQuery(id+"F35.wireOp",EDGE,"E124.sketch_text.stroke-127"),sQuery(id+"F35.wireOp",EDGE,"E124.sketch_text.stroke-128"),sQuery(id+"F35.wireOp",EDGE,"E124.sketch_text.stroke-129"),sQuery(id+"F35.wireOp",EDGE,"E124.sketch_text.stroke-130"),sQuery(id+"F35.wireOp",EDGE,"E124.sketch_text.stroke-131"),sQuery(id+"F35.wireOp",EDGE,"E124.sketch_text.stroke-132")])],"isStart":false})});
            chamfer(context, id + "F37", {"entities" : qUnion([Q0, Q1, Q2, Q3, Q4, Q5, Q6, Q7, Q8, Q9, Q10, Q11]), "width" : .5 * mm, "tangentPropagation" : true});
        }
        {
            var Q0;
            Q0=qCreatedBy(makeId("Top.planeOp"),FACE);
            var sketch = newSketch(context, id + "F38", { "sketchPlane" : qUnion([Q0])});
            skLineSegment(sketch, "E125", {"start": v(-36.82, -29.56) * mm, "end": v(-36.82, -23.16) * mm});
            skLineSegment(sketch, "E126", {"start": v(-36.82, -23.16) * mm, "end": v(14.18, -23.16) * mm});
            skLineSegment(sketch, "E127", {"start": v(14.18, -23.16) * mm, "end": v(14.18, -99.16) * mm});
            skLineSegment(sketch, "E128", {"start": v(14.18, -99.16) * mm, "end": v(7.78, -99.16) * mm});
            skLineSegment(sketch, "E129", {"start": v(7.78, -99.16) * mm, "end": v(7.78, -29.56) * mm});
            skLineSegment(sketch, "E130", {"start": v(7.78, -29.56) * mm, "end": v(-36.82, -29.56) * mm});
            skSolve(sketch);
        }
        {
            var Q0;
            Q0 = qSketchRegion(id + "F38", true);
            extrude(context, id + "F39", {"entities" : qUnion([Q0]), "depth" : 70 * mm});
        }
        {
            var Q0;
            Q0=makeQuery(id+"F39.opExtrude","SWEPT_FACE",FACE,{"disambiguationData":[OSD([sQuery(id+"F38.wireOp",EDGE,"E126")])]});
            var sketch = newSketch(context, id + "F40", { "sketchPlane" : qUnion([Q0])});
            skLineSegment(sketch, "E131", {"start": v(-14.18, 70) * mm, "end": v(5.82, 70) * mm, "construction": true});
            skLineSegment(sketch, "E132", {"start": v(5.82, 70) * mm, "end": v(5.82, 50) * mm, "construction": true});
            skCircle(sketch, "E133", {"center": v(5.82, 50) * mm, "radius": 4.05 * mm});
            skSolve(sketch);
        }
        {
            var Q0;
            Q0 = qSketchRegion(id + "F40", true);
            extrude(context, id + "F41", {"entities" : qUnion([Q0]), "operationType" : NewBodyOperationType.REMOVE, "oppositeDirection" : true, "depth" : 25 * mm});
        }
        {
            var Q0;
            Q0=makeQuery(id+"F39.opExtrude","SWEPT_FACE",FACE,{"disambiguationData":[OSD([sQuery(id+"F38.wireOp",EDGE,"E127")])]});
            var sketch = newSketch(context, id + "F42", { "sketchPlane" : qUnion([Q0])});
            skLineSegment(sketch, "E134", {"start": v(-99.16, 70) * mm, "end": v(-89.16, 70) * mm, "construction": true});
            skLineSegment(sketch, "E135", {"start": v(-89.16, 70) * mm, "end": v(-89.16, 60) * mm, "construction": true});
            skLineSegment(sketch, "E136", {"start": v(-99.16, 0) * mm, "end": v(-89.16, 0) * mm, "construction": true});
            skLineSegment(sketch, "E137", {"start": v(-89.16, 0) * mm, "end": v(-89.16, 10) * mm, "construction": true});
            skCircle(sketch, "E138", {"center": v(-89.16, 60) * mm, "radius": 2.6 * mm});
            skCircle(sketch, "E139", {"center": v(-89.16, 10) * mm, "radius": 2.6 * mm});
            skLineSegment(sketch, "E140", {"start": v(-99.16, 0) * mm, "end": v(-77.66, 0) * mm, "construction": true});
            skLineSegment(sketch, "E141", {"start": v(-77.66, 0) * mm, "end": v(-77.66, 10) * mm, "construction": true});
            skCircle(sketch, "E142", {"center": v(-77.66, 10) * mm, "radius": 1.7 * mm});
            skLineSegment(sketch, "E143", {"start": v(-99.16, 0) * mm, "end": v(-48.16, 0) * mm, "construction": true});
            skLineSegment(sketch, "E144", {"start": v(-48.16, 0) * mm, "end": v(-48.16, 7) * mm, "construction": true});
            skCircle(sketch, "E145", {"center": v(-48.16, 7) * mm, "radius": 2 * mm});
            skLineSegment(sketch, "E146", {"start": v(-99.16, 70) * mm, "end": v(-77.66, 70) * mm, "construction": true});
            skLineSegment(sketch, "E147", {"start": v(-77.66, 70) * mm, "end": v(-77.66, 60) * mm, "construction": true});
            skCircle(sketch, "E148", {"center": v(-77.66, 60) * mm, "radius": 1.7 * mm});
            skSolve(sketch);
        }
        {
            var Q0;
            Q0 = qSketchRegion(id + "F42", true);
            extrude(context, id + "F43", {"entities" : qUnion([Q0]), "operationType" : NewBodyOperationType.REMOVE, "oppositeDirection" : true, "depth" : 25 * mm});
        }
        {
            var Q0;
            Q0=makeQuery(id+"F39.opExtrude","SWEPT_FACE",FACE,{"disambiguationData":[OSD([sQuery(id+"F38.wireOp",EDGE,"E127")])]});
            var sketch = newSketch(context, id + "F44", { "sketchPlane" : qUnion([Q0])});
            skText(sketch, "E149", { "text": "v0.1 RC1.0\nB,L", "fontName": "OpenSans-Bold.ttf"});
            const initialGuessF44  = {"E149": [-0.0965, 0.0416, 1, 0, 0.01006]};
            skSetInitialGuess(sketch, initialGuessF44);
            skSolve(sketch);
        }
        {
            var Q0;
            Q0 = qSketchRegion(id + "F44", true);
            extrude(context, id + "F45", {"entities" : qUnion([Q0]), "operationType" : NewBodyOperationType.REMOVE, "oppositeDirection" : true, "depth" : .5 * mm});
        }
        {
            var Q0;
            Q0=makeQuery(id+"F45.boolean.opBoolean","COPY",FACE,{"derivedFrom":makeQuery(id+"F45.opExtrude","CAP_FACE",FACE,{"disambiguationData":[OSD([sQuery(id+"F44.wireOp",EDGE,"E149.sketch_text.stroke-0"),sQuery(id+"F44.wireOp",EDGE,"E149.sketch_text.stroke-1"),sQuery(id+"F44.wireOp",EDGE,"E149.sketch_text.stroke-2"),sQuery(id+"F44.wireOp",EDGE,"E149.sketch_text.stroke-3"),sQuery(id+"F44.wireOp",EDGE,"E149.sketch_text.stroke-4"),sQuery(id+"F44.wireOp",EDGE,"E149.sketch_text.stroke-5"),sQuery(id+"F44.wireOp",EDGE,"E149.sketch_text.stroke-6"),sQuery(id+"F44.wireOp",EDGE,"E149.sketch_text.stroke-7"),sQuery(id+"F44.wireOp",EDGE,"E149.sketch_text.stroke-8"),sQuery(id+"F44.wireOp",EDGE,"E149.sketch_text.stroke-9")])],"isStart":false})});
            var Q1;
            Q1=makeQuery(id+"F45.boolean.opBoolean","COPY",FACE,{"derivedFrom":makeQuery(id+"F45.opExtrude","CAP_FACE",FACE,{"disambiguationData":[OSD([sQuery(id+"F44.wireOp",EDGE,"E149.sketch_text.stroke-10"),sQuery(id+"F44.wireOp",EDGE,"E149.sketch_text.stroke-11"),sQuery(id+"F44.wireOp",EDGE,"E149.sketch_text.stroke-12"),sQuery(id+"F44.wireOp",EDGE,"E149.sketch_text.stroke-13"),sQuery(id+"F44.wireOp",EDGE,"E149.sketch_text.stroke-14"),sQuery(id+"F44.wireOp",EDGE,"E149.sketch_text.stroke-15"),sQuery(id+"F44.wireOp",EDGE,"E149.sketch_text.stroke-16"),sQuery(id+"F44.wireOp",EDGE,"E149.sketch_text.stroke-17"),sQuery(id+"F44.wireOp",EDGE,"E149.sketch_text.stroke-18"),sQuery(id+"F44.wireOp",EDGE,"E149.sketch_text.stroke-19"),sQuery(id+"F44.wireOp",EDGE,"E149.sketch_text.stroke-20"),sQuery(id+"F44.wireOp",EDGE,"E149.sketch_text.stroke-21"),sQuery(id+"F44.wireOp",EDGE,"E149.sketch_text.stroke-22"),sQuery(id+"F44.wireOp",EDGE,"E149.sketch_text.stroke-23"),sQuery(id+"F44.wireOp",EDGE,"E149.sketch_text.stroke-24"),sQuery(id+"F44.wireOp",EDGE,"E149.sketch_text.stroke-25")])],"isStart":false})});
            var Q2;
            Q2=makeQuery(id+"F45.boolean.opBoolean","COPY",FACE,{"derivedFrom":makeQuery(id+"F45.opExtrude","CAP_FACE",FACE,{"disambiguationData":[OSD([sQuery(id+"F44.wireOp",EDGE,"E149.sketch_text.stroke-26"),sQuery(id+"F44.wireOp",EDGE,"E149.sketch_text.stroke-27"),sQuery(id+"F44.wireOp",EDGE,"E149.sketch_text.stroke-28"),sQuery(id+"F44.wireOp",EDGE,"E149.sketch_text.stroke-29"),sQuery(id+"F44.wireOp",EDGE,"E149.sketch_text.stroke-30"),sQuery(id+"F44.wireOp",EDGE,"E149.sketch_text.stroke-31"),sQuery(id+"F44.wireOp",EDGE,"E149.sketch_text.stroke-32"),sQuery(id+"F44.wireOp",EDGE,"E149.sketch_text.stroke-33")])],"isStart":false})});
            var Q3;
            Q3=makeQuery(id+"F45.boolean.opBoolean","COPY",FACE,{"derivedFrom":makeQuery(id+"F45.opExtrude","CAP_FACE",FACE,{"disambiguationData":[OSD([sQuery(id+"F44.wireOp",EDGE,"E149.sketch_text.stroke-34"),sQuery(id+"F44.wireOp",EDGE,"E149.sketch_text.stroke-35"),sQuery(id+"F44.wireOp",EDGE,"E149.sketch_text.stroke-36"),sQuery(id+"F44.wireOp",EDGE,"E149.sketch_text.stroke-37"),sQuery(id+"F44.wireOp",EDGE,"E149.sketch_text.stroke-38"),sQuery(id+"F44.wireOp",EDGE,"E149.sketch_text.stroke-39"),sQuery(id+"F44.wireOp",EDGE,"E149.sketch_text.stroke-40"),sQuery(id+"F44.wireOp",EDGE,"E149.sketch_text.stroke-41"),sQuery(id+"F44.wireOp",EDGE,"E149.sketch_text.stroke-42"),sQuery(id+"F44.wireOp",EDGE,"E149.sketch_text.stroke-43")])],"isStart":false})});
            var Q4;
            Q4=makeQuery(id+"F45.boolean.opBoolean","COPY",FACE,{"derivedFrom":makeQuery(id+"F45.opExtrude","CAP_FACE",FACE,{"disambiguationData":[OSD([sQuery(id+"F44.wireOp",EDGE,"E149.sketch_text.stroke-44"),sQuery(id+"F44.wireOp",EDGE,"E149.sketch_text.stroke-45"),sQuery(id+"F44.wireOp",EDGE,"E149.sketch_text.stroke-46"),sQuery(id+"F44.wireOp",EDGE,"E149.sketch_text.stroke-47"),sQuery(id+"F44.wireOp",EDGE,"E149.sketch_text.stroke-48"),sQuery(id+"F44.wireOp",EDGE,"E149.sketch_text.stroke-49"),sQuery(id+"F44.wireOp",EDGE,"E149.sketch_text.stroke-50"),sQuery(id+"F44.wireOp",EDGE,"E149.sketch_text.stroke-51"),sQuery(id+"F44.wireOp",EDGE,"E149.sketch_text.stroke-52"),sQuery(id+"F44.wireOp",EDGE,"E149.sketch_text.stroke-53"),sQuery(id+"F44.wireOp",EDGE,"E149.sketch_text.stroke-54"),sQuery(id+"F44.wireOp",EDGE,"E149.sketch_text.stroke-55"),sQuery(id+"F44.wireOp",EDGE,"E149.sketch_text.stroke-56"),sQuery(id+"F44.wireOp",EDGE,"E149.sketch_text.stroke-57"),sQuery(id+"F44.wireOp",EDGE,"E149.sketch_text.stroke-58"),sQuery(id+"F44.wireOp",EDGE,"E149.sketch_text.stroke-59"),sQuery(id+"F44.wireOp",EDGE,"E149.sketch_text.stroke-60"),sQuery(id+"F44.wireOp",EDGE,"E149.sketch_text.stroke-61"),sQuery(id+"F44.wireOp",EDGE,"E149.sketch_text.stroke-62")])],"isStart":false})});
            var Q5;
            Q5=makeQuery(id+"F45.boolean.opBoolean","COPY",FACE,{"derivedFrom":makeQuery(id+"F45.opExtrude","CAP_FACE",FACE,{"disambiguationData":[OSD([sQuery(id+"F44.wireOp",EDGE,"E149.sketch_text.stroke-63"),sQuery(id+"F44.wireOp",EDGE,"E149.sketch_text.stroke-64"),sQuery(id+"F44.wireOp",EDGE,"E149.sketch_text.stroke-65"),sQuery(id+"F44.wireOp",EDGE,"E149.sketch_text.stroke-66"),sQuery(id+"F44.wireOp",EDGE,"E149.sketch_text.stroke-67"),sQuery(id+"F44.wireOp",EDGE,"E149.sketch_text.stroke-68"),sQuery(id+"F44.wireOp",EDGE,"E149.sketch_text.stroke-69"),sQuery(id+"F44.wireOp",EDGE,"E149.sketch_text.stroke-70"),sQuery(id+"F44.wireOp",EDGE,"E149.sketch_text.stroke-71"),sQuery(id+"F44.wireOp",EDGE,"E149.sketch_text.stroke-72"),sQuery(id+"F44.wireOp",EDGE,"E149.sketch_text.stroke-73"),sQuery(id+"F44.wireOp",EDGE,"E149.sketch_text.stroke-74"),sQuery(id+"F44.wireOp",EDGE,"E149.sketch_text.stroke-75"),sQuery(id+"F44.wireOp",EDGE,"E149.sketch_text.stroke-76"),sQuery(id+"F44.wireOp",EDGE,"E149.sketch_text.stroke-77")])],"isStart":false})});
            var Q6;
            Q6=makeQuery(id+"F45.boolean.opBoolean","COPY",FACE,{"derivedFrom":makeQuery(id+"F45.opExtrude","CAP_FACE",FACE,{"disambiguationData":[OSD([sQuery(id+"F44.wireOp",EDGE,"E149.sketch_text.stroke-78"),sQuery(id+"F44.wireOp",EDGE,"E149.sketch_text.stroke-79"),sQuery(id+"F44.wireOp",EDGE,"E149.sketch_text.stroke-80"),sQuery(id+"F44.wireOp",EDGE,"E149.sketch_text.stroke-81"),sQuery(id+"F44.wireOp",EDGE,"E149.sketch_text.stroke-82"),sQuery(id+"F44.wireOp",EDGE,"E149.sketch_text.stroke-83"),sQuery(id+"F44.wireOp",EDGE,"E149.sketch_text.stroke-84"),sQuery(id+"F44.wireOp",EDGE,"E149.sketch_text.stroke-85"),sQuery(id+"F44.wireOp",EDGE,"E149.sketch_text.stroke-86"),sQuery(id+"F44.wireOp",EDGE,"E149.sketch_text.stroke-87")])],"isStart":false})});
            var Q7;
            Q7=makeQuery(id+"F45.boolean.opBoolean","COPY",FACE,{"derivedFrom":makeQuery(id+"F45.opExtrude","CAP_FACE",FACE,{"disambiguationData":[OSD([sQuery(id+"F44.wireOp",EDGE,"E149.sketch_text.stroke-88"),sQuery(id+"F44.wireOp",EDGE,"E149.sketch_text.stroke-89"),sQuery(id+"F44.wireOp",EDGE,"E149.sketch_text.stroke-90"),sQuery(id+"F44.wireOp",EDGE,"E149.sketch_text.stroke-91"),sQuery(id+"F44.wireOp",EDGE,"E149.sketch_text.stroke-92"),sQuery(id+"F44.wireOp",EDGE,"E149.sketch_text.stroke-93"),sQuery(id+"F44.wireOp",EDGE,"E149.sketch_text.stroke-94"),sQuery(id+"F44.wireOp",EDGE,"E149.sketch_text.stroke-95")])],"isStart":false})});
            var Q8;
            Q8=makeQuery(id+"F45.boolean.opBoolean","COPY",FACE,{"derivedFrom":makeQuery(id+"F45.opExtrude","CAP_FACE",FACE,{"disambiguationData":[OSD([sQuery(id+"F44.wireOp",EDGE,"E149.sketch_text.stroke-96"),sQuery(id+"F44.wireOp",EDGE,"E149.sketch_text.stroke-97"),sQuery(id+"F44.wireOp",EDGE,"E149.sketch_text.stroke-98"),sQuery(id+"F44.wireOp",EDGE,"E149.sketch_text.stroke-99"),sQuery(id+"F44.wireOp",EDGE,"E149.sketch_text.stroke-100"),sQuery(id+"F44.wireOp",EDGE,"E149.sketch_text.stroke-101"),sQuery(id+"F44.wireOp",EDGE,"E149.sketch_text.stroke-102"),sQuery(id+"F44.wireOp",EDGE,"E149.sketch_text.stroke-103"),sQuery(id+"F44.wireOp",EDGE,"E149.sketch_text.stroke-104"),sQuery(id+"F44.wireOp",EDGE,"E149.sketch_text.stroke-105"),sQuery(id+"F44.wireOp",EDGE,"E149.sketch_text.stroke-106"),sQuery(id+"F44.wireOp",EDGE,"E149.sketch_text.stroke-107"),sQuery(id+"F44.wireOp",EDGE,"E149.sketch_text.stroke-108"),sQuery(id+"F44.wireOp",EDGE,"E149.sketch_text.stroke-109"),sQuery(id+"F44.wireOp",EDGE,"E149.sketch_text.stroke-110"),sQuery(id+"F44.wireOp",EDGE,"E149.sketch_text.stroke-111")])],"isStart":false})});
            var Q9;
            Q9=makeQuery(id+"F45.boolean.opBoolean","COPY",FACE,{"derivedFrom":makeQuery(id+"F45.opExtrude","CAP_FACE",FACE,{"disambiguationData":[OSD([sQuery(id+"F44.wireOp",EDGE,"E149.sketch_text.stroke-112"),sQuery(id+"F44.wireOp",EDGE,"E149.sketch_text.stroke-113"),sQuery(id+"F44.wireOp",EDGE,"E149.sketch_text.stroke-114"),sQuery(id+"F44.wireOp",EDGE,"E149.sketch_text.stroke-115"),sQuery(id+"F44.wireOp",EDGE,"E149.sketch_text.stroke-116"),sQuery(id+"F44.wireOp",EDGE,"E149.sketch_text.stroke-117"),sQuery(id+"F44.wireOp",EDGE,"E149.sketch_text.stroke-118"),sQuery(id+"F44.wireOp",EDGE,"E149.sketch_text.stroke-119"),sQuery(id+"F44.wireOp",EDGE,"E149.sketch_text.stroke-120"),sQuery(id+"F44.wireOp",EDGE,"E149.sketch_text.stroke-121"),sQuery(id+"F44.wireOp",EDGE,"E149.sketch_text.stroke-122"),sQuery(id+"F44.wireOp",EDGE,"E149.sketch_text.stroke-123"),sQuery(id+"F44.wireOp",EDGE,"E149.sketch_text.stroke-124"),sQuery(id+"F44.wireOp",EDGE,"E149.sketch_text.stroke-125"),sQuery(id+"F44.wireOp",EDGE,"E149.sketch_text.stroke-126"),sQuery(id+"F44.wireOp",EDGE,"E149.sketch_text.stroke-127"),sQuery(id+"F44.wireOp",EDGE,"E149.sketch_text.stroke-128"),sQuery(id+"F44.wireOp",EDGE,"E149.sketch_text.stroke-129"),sQuery(id+"F44.wireOp",EDGE,"E149.sketch_text.stroke-130"),sQuery(id+"F44.wireOp",EDGE,"E149.sketch_text.stroke-131"),sQuery(id+"F44.wireOp",EDGE,"E149.sketch_text.stroke-132"),sQuery(id+"F44.wireOp",EDGE,"E149.sketch_text.stroke-133"),sQuery(id+"F44.wireOp",EDGE,"E149.sketch_text.stroke-134"),sQuery(id+"F44.wireOp",EDGE,"E149.sketch_text.stroke-135"),sQuery(id+"F44.wireOp",EDGE,"E149.sketch_text.stroke-136")])],"isStart":false})});
            var Q10;
            Q10=makeQuery(id+"F45.boolean.opBoolean","COPY",FACE,{"derivedFrom":makeQuery(id+"F45.opExtrude","CAP_FACE",FACE,{"disambiguationData":[OSD([sQuery(id+"F44.wireOp",EDGE,"E149.sketch_text.stroke-137"),sQuery(id+"F44.wireOp",EDGE,"E149.sketch_text.stroke-138"),sQuery(id+"F44.wireOp",EDGE,"E149.sketch_text.stroke-139"),sQuery(id+"F44.wireOp",EDGE,"E149.sketch_text.stroke-140"),sQuery(id+"F44.wireOp",EDGE,"E149.sketch_text.stroke-141")])],"isStart":false})});
            var Q11;
            Q11=makeQuery(id+"F45.boolean.opBoolean","COPY",FACE,{"derivedFrom":makeQuery(id+"F45.opExtrude","CAP_FACE",FACE,{"disambiguationData":[OSD([sQuery(id+"F44.wireOp",EDGE,"E149.sketch_text.stroke-142"),sQuery(id+"F44.wireOp",EDGE,"E149.sketch_text.stroke-143"),sQuery(id+"F44.wireOp",EDGE,"E149.sketch_text.stroke-144"),sQuery(id+"F44.wireOp",EDGE,"E149.sketch_text.stroke-145"),sQuery(id+"F44.wireOp",EDGE,"E149.sketch_text.stroke-146"),sQuery(id+"F44.wireOp",EDGE,"E149.sketch_text.stroke-147")])],"isStart":false})});
            chamfer(context, id + "F46", {"entities" : qUnion([Q0, Q1, Q2, Q3, Q4, Q5, Q6, Q7, Q8, Q9, Q10, Q11]), "width" : .5 * mm, "tangentPropagation" : true});
        }
    });
